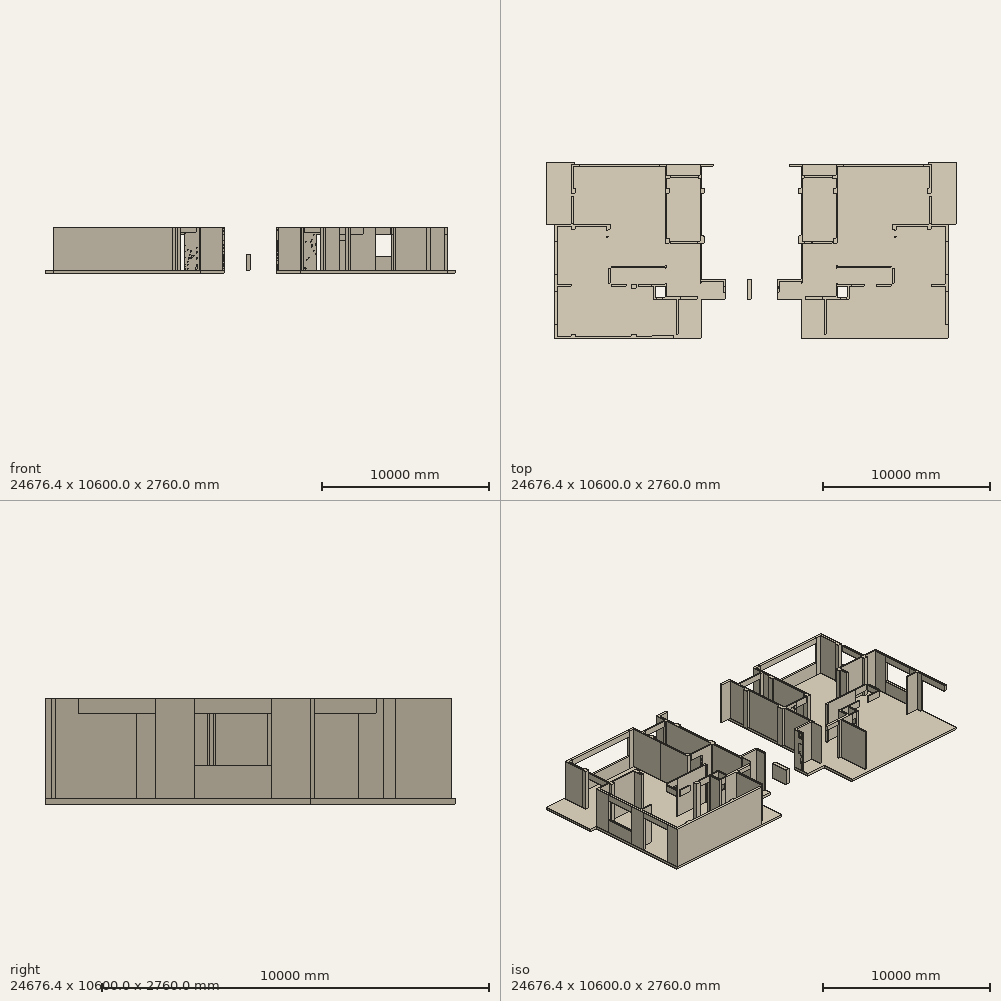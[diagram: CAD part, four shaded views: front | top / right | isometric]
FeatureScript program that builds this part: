
annotation { "Feature Type Name" : "Feature", "Feature Type Description" : "" }
export const myFeature = defineFeature(function(context is Context, id is Id, definition is map)
    precondition{}
    {
        {
            var Q0;
            Q0=qCreatedBy(makeId("Top.planeOp"),FACE);
            var sketch = newSketch(context, id + "F0", { "sketchPlane" : qUnion([Q0])});
            skLineSegment(sketch, "E0", {"start": v(-129.87, 2534.85) * mm, "end": v(8420.13, 2534.85) * mm});
            skLineSegment(sketch, "E1", {"start": v(-1879.16, 934.85) * mm, "end": v(11256.98, 934.85) * mm, "construction": true});
            skLineSegment(sketch, "E2", {"start": v(0, 1773.33) * mm, "end": v(0, -9278.74) * mm, "construction": true});
            skLineSegment(sketch, "E3", {"start": v(5650, -9203.63) * mm, "end": v(5650, -7807.62) * mm, "construction": true});
            skLineSegment(sketch, "E4.bottom", {"start": v(-125, 1084.85) * mm, "end": v(125, 1084.85) * mm});
            skLineSegment(sketch, "E4.top", {"start": v(-125, 784.85) * mm, "end": v(125, 784.85) * mm});
            skLineSegment(sketch, "E4.left", {"start": v(-125, 1084.85) * mm, "end": v(-125, 784.85) * mm});
            skLineSegment(sketch, "E4.right", {"start": v(125, 1084.85) * mm, "end": v(125, 784.85) * mm});
            skLineSegment(sketch, "E5.bottom", {"start": v(-125, 784.85) * mm, "end": v(-25, 784.85) * mm});
            skLineSegment(sketch, "E5.top", {"start": v(-125, 584.85) * mm, "end": v(-25, 584.85) * mm});
            skLineSegment(sketch, "E5.left", {"start": v(-125, 784.85) * mm, "end": v(-125, 584.85) * mm});
            skLineSegment(sketch, "E5.right", {"start": v(-25, 784.85) * mm, "end": v(-25, 584.85) * mm});
            skLineSegment(sketch, "E6.left", {"start": v(-125, 1084.85) * mm, "end": v(-129.87, 2534.85) * mm});
            skLineSegment(sketch, "E7.bottom", {"start": v(-129.87, 2534.85) * mm, "end": v(5170.13, 2534.85) * mm});
            skLineSegment(sketch, "E7.top", {"start": v(25, 2384.85) * mm, "end": v(5170.13, 2384.85) * mm});
            skLineSegment(sketch, "E7.right", {"start": v(5170.13, 2534.85) * mm, "end": v(5170.13, 2384.85) * mm});
            skLineSegment(sketch, "E8", {"start": v(370.13, 2534.85) * mm, "end": v(370.13, 2384.85) * mm});
            skLineSegment(sketch, "E9", {"start": v(5520.13, 2384.85) * mm, "end": v(5520.13, 126.86) * mm});
            skLineSegment(sketch, "E10", {"start": v(5520.13, 2534.85) * mm, "end": v(5620.13, 2534.85) * mm});
            skLineSegment(sketch, "E11", {"start": v(5620.13, 2534.85) * mm, "end": v(5620.13, 1834.85) * mm});
            skLineSegment(sketch, "E12", {"start": v(5620.13, 1834.85) * mm, "end": v(7620.13, 1834.85) * mm});
            skLineSegment(sketch, "E13", {"start": v(5620.13, 1684.85) * mm, "end": v(7725, 1684.85) * mm});
            skLineSegment(sketch, "E14", {"start": v(5620.13, 1684.85) * mm, "end": v(5620.13, 1084.85) * mm});
            skLineSegment(sketch, "E15.bottom", {"start": v(5520.13, 1084.85) * mm, "end": v(5859.5, 1084.85) * mm});
            skLineSegment(sketch, "E16", {"start": v(5170.13, 2384.85) * mm, "end": v(5520.13, 2384.85) * mm});
            skLineSegment(sketch, "E17.bottom", {"start": v(5520.13, 1084.85) * mm, "end": v(5770.13, 1084.85) * mm});
            skLineSegment(sketch, "E18", {"start": v(7620.13, 1834.85) * mm, "end": v(7620.13, 2534.85) * mm});
            skLineSegment(sketch, "E19", {"start": v(5820.13, 1684.85) * mm, "end": v(5820.13, 1834.85) * mm});
            skLineSegment(sketch, "E20", {"start": v(6720.13, 1684.85) * mm, "end": v(6720.13, 1834.85) * mm});
            skLineSegment(sketch, "E21", {"start": v(7520.13, 1834.85) * mm, "end": v(7520.13, 1684.85) * mm});
            skLineSegment(sketch, "E22", {"start": v(7720.13, 2384.85) * mm, "end": v(7720.13, 1084.85) * mm});
            skLineSegment(sketch, "E23", {"start": v(7720.13, 2384.85) * mm, "end": v(8420.13, 2384.85) * mm});
            skLineSegment(sketch, "E24", {"start": v(8420.13, 2534.85) * mm, "end": v(8420.13, 2384.85) * mm});
            skLineSegment(sketch, "E25", {"start": v(5520.13, 784.85) * mm, "end": v(5650, 784.85) * mm});
            skLineSegment(sketch, "E26", {"start": v(5650, 784.85) * mm, "end": v(5859.5, 784.85) * mm});
            skLineSegment(sketch, "E27.bottom", {"start": v(7725, 1084.85) * mm, "end": v(7875, 1084.85) * mm});
            skLineSegment(sketch, "E27.top", {"start": v(7725, 784.85) * mm, "end": v(7875, 784.85) * mm});
            skLineSegment(sketch, "E28", {"start": v(5620.13, 784.85) * mm, "end": v(5620.13, -143.22) * mm});
            skLineSegment(sketch, "E29", {"start": v(0, -1115.15) * mm, "end": v(2222.83, -1115.15) * mm});
            skLineSegment(sketch, "E30.top", {"start": v(-125, -1115.15) * mm, "end": v(-25, -1115.15) * mm});
            skLineSegment(sketch, "E30.left", {"start": v(-125, 584.85) * mm, "end": v(-125, -1115.15) * mm});
            skLineSegment(sketch, "E30.right", {"start": v(-25, 584.85) * mm, "end": v(-25, -1115.15) * mm});
            skLineSegment(sketch, "E31.top", {"start": v(-125, -1015.15) * mm, "end": v(-25, -1015.15) * mm});
            skLineSegment(sketch, "E31.left", {"start": v(-125, -1115.15) * mm, "end": v(-125, -1015.15) * mm});
            skLineSegment(sketch, "E31.right", {"start": v(-25, -1115.15) * mm, "end": v(-25, -1015.15) * mm});
            skLineSegment(sketch, "E32", {"start": v(-125, -115.15) * mm, "end": v(-25, -115.15) * mm});
            skLineSegment(sketch, "E33", {"start": v(-125, -1115.15) * mm, "end": v(-1125, -1115.15) * mm});
            skLineSegment(sketch, "E34", {"start": v(-1125, -1115.15) * mm, "end": v(-1125, -2115.15) * mm});
            skLineSegment(sketch, "E35", {"start": v(-975, -1215.15) * mm, "end": v(1972.83, -1215.15) * mm});
            skLineSegment(sketch, "E36.bottom", {"start": v(-125, -1115.15) * mm, "end": v(125, -1115.15) * mm});
            skLineSegment(sketch, "E36.top", {"start": v(-125, -1415.15) * mm, "end": v(125, -1415.15) * mm});
            skLineSegment(sketch, "E36.left", {"start": v(-125, -1115.15) * mm, "end": v(-125, -1415.15) * mm});
            skLineSegment(sketch, "E36.right", {"start": v(125, -1115.15) * mm, "end": v(125, -1415.15) * mm});
            skLineSegment(sketch, "E37", {"start": v(2222.83, -3615.15) * mm, "end": v(2222.83, -1115.15) * mm});
            skLineSegment(sketch, "E38", {"start": v(2122.83, -1415.15) * mm, "end": v(2122.83, -4715.15) * mm});
            skLineSegment(sketch, "E39.bottom", {"start": v(2222.83, -1115.15) * mm, "end": v(1972.83, -1115.15) * mm});
            skLineSegment(sketch, "E39.top", {"start": v(2222.83, -1415.15) * mm, "end": v(1972.83, -1415.15) * mm});
            skLineSegment(sketch, "E39.left", {"start": v(2222.83, -1115.15) * mm, "end": v(2222.83, -1415.15) * mm});
            skLineSegment(sketch, "E39.right", {"start": v(1972.83, -1115.15) * mm, "end": v(1972.83, -1415.15) * mm});
            skLineSegment(sketch, "E40", {"start": v(-129.87, 2534.85) * mm, "end": v(138.86, 2534.85) * mm});
            skLineSegment(sketch, "E41", {"start": v(25, 2634.85) * mm, "end": v(-1629.87, 2634.85) * mm});
            skLineSegment(sketch, "E42", {"start": v(25, 2534.85) * mm, "end": v(25, 2634.85) * mm});
            skLineSegment(sketch, "E43", {"start": v(-1125, -1115.15) * mm, "end": v(-1629.87, -1115.15) * mm});
            skLineSegment(sketch, "E44", {"start": v(-1629.87, -1115.15) * mm, "end": v(-1629.87, 2634.85) * mm});
            skLineSegment(sketch, "E45", {"start": v(-979.87, -4715.15) * mm, "end": v(2122.83, -4715.15) * mm});
            skLineSegment(sketch, "E46.bottom", {"start": v(-1125, -2115.15) * mm, "end": v(-979.87, -2115.15) * mm});
            skLineSegment(sketch, "E46.top", {"start": v(-1125, -4115.15) * mm, "end": v(-979.87, -4115.15) * mm});
            skLineSegment(sketch, "E46.left", {"start": v(-1125, -2115.15) * mm, "end": v(-1125, -4115.15) * mm});
            skLineSegment(sketch, "E46.right", {"start": v(-979.87, -2115.15) * mm, "end": v(-979.87, -4115.15) * mm});
            skLineSegment(sketch, "E47", {"start": v(-975, -1215.15) * mm, "end": v(-979.87, -2115.15) * mm});
            skLineSegment(sketch, "E48.top", {"start": v(-1125, -5115.15) * mm, "end": v(-979.87, -5115.15) * mm});
            skLineSegment(sketch, "E48.left", {"start": v(-1125, -4115.15) * mm, "end": v(-1125, -5115.15) * mm});
            skLineSegment(sketch, "E48.right", {"start": v(-979.87, -4115.15) * mm, "end": v(-979.87, -5115.15) * mm});
            skLineSegment(sketch, "E49.bottom", {"start": v(-979.87, -5115.15) * mm, "end": v(-1125, -5115.15) * mm});
            skLineSegment(sketch, "E49.top", {"start": v(-979.87, -7115.15) * mm, "end": v(-1125, -7115.15) * mm});
            skLineSegment(sketch, "E49.left", {"start": v(-979.87, -5115.15) * mm, "end": v(-979.87, -7115.15) * mm});
            skLineSegment(sketch, "E49.right", {"start": v(-1125, -5115.15) * mm, "end": v(-1125, -7115.15) * mm});
            skLineSegment(sketch, "E50.bottom", {"start": v(-1125, -7115.15) * mm, "end": v(-975, -7115.15) * mm});
            skLineSegment(sketch, "E50.left", {"start": v(-1125, -7115.15) * mm, "end": v(-1125, -7965.15) * mm});
            skLineSegment(sketch, "E50.right", {"start": v(-975, -7115.15) * mm, "end": v(-975, -7815.15) * mm});
            skLineSegment(sketch, "E51", {"start": v(-979.87, -4815.15) * mm, "end": v(-150, -4815.15) * mm});
            skLineSegment(sketch, "E52", {"start": v(2222.83, -3715.15) * mm, "end": v(2222.83, -4715.15) * mm});
            skLineSegment(sketch, "E53.bottom", {"start": v(-150, -4715.15) * mm, "end": v(150, -4715.15) * mm});
            skLineSegment(sketch, "E53.top", {"start": v(-150, -4965.15) * mm, "end": v(150, -4965.15) * mm});
            skLineSegment(sketch, "E53.left", {"start": v(-150, -4715.15) * mm, "end": v(-150, -4965.15) * mm});
            skLineSegment(sketch, "E53.right", {"start": v(150, -4715.15) * mm, "end": v(150, -4965.15) * mm});
            skLineSegment(sketch, "E54.bottom", {"start": v(-150, -7965.15) * mm, "end": v(150, -7965.15) * mm});
            skLineSegment(sketch, "E54.top", {"start": v(-150, -7715.15) * mm, "end": v(150, -7715.15) * mm});
            skLineSegment(sketch, "E54.left", {"start": v(-150, -7965.15) * mm, "end": v(-150, -7715.15) * mm});
            skLineSegment(sketch, "E54.right", {"start": v(150, -7965.15) * mm, "end": v(150, -7715.15) * mm});
            skLineSegment(sketch, "E55.trimOffspring", {"start": v(-150, -7815.15) * mm, "end": v(-975, -7815.15) * mm});
            skPoint(sketch, "E56.startSnap0", {"position": v(2222.83, -4215.15) * mm});
            skLineSegment(sketch, "E57", {"start": v(3220.13, -4815.15) * mm, "end": v(3220.13, -7815.15) * mm});
            skLineSegment(sketch, "E58", {"start": v(150, -4815.15) * mm, "end": v(3520.13, -4815.15) * mm});
            skLineSegment(sketch, "E59", {"start": v(2222.83, -4715.15) * mm, "end": v(5520.13, -4715.15) * mm});
            skLineSegment(sketch, "E60.trimOffspring", {"start": v(3820.13, -4815.15) * mm, "end": v(4820.13, -4815.15) * mm});
            skLineSegment(sketch, "E61", {"start": v(150, -7815.15) * mm, "end": v(3520.13, -7815.15) * mm});
            skLineSegment(sketch, "E62", {"start": v(3820.13, -4815.15) * mm, "end": v(3820.13, -7814.9) * mm});
            skLineSegment(sketch, "E63", {"start": v(3720.13, -4965.15) * mm, "end": v(3720.13, -7715.15) * mm});
            skLineSegment(sketch, "E64", {"start": v(-1125, -7965.15) * mm, "end": v(6320.13, -7965.15) * mm});
            skLineSegment(sketch, "E65", {"start": v(6320.13, -5615.15) * mm, "end": v(6320.13, -7804.95) * mm});
            skLineSegment(sketch, "E66", {"start": v(3820.13, -7814.9) * mm, "end": v(6020.13, -7806.15) * mm});
            skLineSegment(sketch, "E67", {"start": v(6220.13, -7715.15) * mm, "end": v(6220.13, -5615.15) * mm});
            skLineSegment(sketch, "E68", {"start": v(7725, 1684.85) * mm, "end": v(7725, 1084.85) * mm});
            skLineSegment(sketch, "E69.left", {"start": v(7725, 1084.85) * mm, "end": v(7725, 784.85) * mm});
            skLineSegment(sketch, "E70", {"start": v(2222.83, -3615.15) * mm, "end": v(5522.83, -3615.15) * mm});
            skLineSegment(sketch, "E71", {"start": v(2222.83, -3715.15) * mm, "end": v(5520.13, -3715.15) * mm});
            skLineSegment(sketch, "E72", {"start": v(5522.83, -3040.95) * mm, "end": v(5522.83, -3615.15) * mm});
            skLineSegment(sketch, "E73", {"start": v(5620.13, -4815.15) * mm, "end": v(5620.13, -2614.3) * mm});
            skPoint(sketch, "E74.trimOffspring.end.orphan", {"position": v(5520.13, -5415.07) * mm});
            skLineSegment(sketch, "E75", {"start": v(5520.13, -4715.15) * mm, "end": v(5520.13, -3715.15) * mm});
            skLineSegment(sketch, "E76", {"start": v(25, 2384.85) * mm, "end": v(25, 1084.85) * mm});
            skLineSegment(sketch, "E77", {"start": v(5520.13, 126.86) * mm, "end": v(5522.83, -3040.95) * mm});
            skLineSegment(sketch, "E78", {"start": v(5620.13, -143.22) * mm, "end": v(5620.13, -1915.15) * mm});
            skLineSegment(sketch, "E79.right", {"start": v(9025, -4814.81) * mm, "end": v(9025, -4539.81) * mm});
            skLineSegment(sketch, "E80", {"start": v(7948.57, -4539.81) * mm, "end": v(9025, -4539.81) * mm});
            skLineSegment(sketch, "E81.bottom", {"start": v(7625, 1084.85) * mm, "end": v(7875, 1084.85) * mm});
            skLineSegment(sketch, "E81.top", {"start": v(7625, 784.85) * mm, "end": v(7875, 784.85) * mm});
            skLineSegment(sketch, "E81.left", {"start": v(7625, 1084.85) * mm, "end": v(7625, 784.85) * mm});
            skLineSegment(sketch, "E81.right", {"start": v(7875, 1084.85) * mm, "end": v(7875, 784.85) * mm});
            skLineSegment(sketch, "E82.right", {"start": v(9025, -4739.81) * mm, "end": v(9025, -4539.81) * mm});
            skLineSegment(sketch, "E83", {"start": v(9125, -4539.81) * mm, "end": v(9125, -4439.81) * mm});
            skLineSegment(sketch, "E84", {"start": v(3920.13, -4715.15) * mm, "end": v(3920.13, -4815.15) * mm});
            skLineSegment(sketch, "E85.bottom", {"start": v(3920.13, -4715.15) * mm, "end": v(4720.13, -4715.15) * mm});
            skLineSegment(sketch, "E85.top", {"start": v(3920.13, -4815.15) * mm, "end": v(4720.13, -4815.15) * mm});
            skLineSegment(sketch, "E85.right", {"start": v(4720.13, -4715.15) * mm, "end": v(4720.13, -4815.15) * mm});
            skLineSegment(sketch, "E86.bottom", {"start": v(4920.13, -4815.15) * mm, "end": v(5520.13, -4815.15) * mm});
            skLineSegment(sketch, "E86.top", {"start": v(4820.13, -5615.15) * mm, "end": v(5520.13, -5615.15) * mm});
            skLineSegment(sketch, "E86.left", {"start": v(4820.13, -4815.15) * mm, "end": v(4820.13, -5615.15) * mm});
            skLineSegment(sketch, "E86.right", {"start": v(5520.13, -4815.15) * mm, "end": v(5520.13, -5515.15) * mm});
            skLineSegment(sketch, "E87.top", {"start": v(4920.13, -5515.15) * mm, "end": v(5520.13, -5515.15) * mm});
            skLineSegment(sketch, "E87.left", {"start": v(4920.13, -4815.15) * mm, "end": v(4920.13, -5515.15) * mm});
            skLineSegment(sketch, "E88.bottom", {"start": v(5520.13, -4815.15) * mm, "end": v(4920.13, -4815.15) * mm});
            skLineSegment(sketch, "E88.top", {"start": v(5620.13, -5615.15) * mm, "end": v(4820.13, -5615.15) * mm});
            skLineSegment(sketch, "E88.left", {"start": v(5620.13, -4815.15) * mm, "end": v(5620.13, -5439.81) * mm});
            skLineSegment(sketch, "E89", {"start": v(5620.13, -5615.15) * mm, "end": v(6220.13, -5615.15) * mm});
            skLineSegment(sketch, "E90.bottom", {"start": v(6320.13, -5615.15) * mm, "end": v(9125, -5615.15) * mm});
            skLineSegment(sketch, "E90.top", {"start": v(6220.13, -5439.81) * mm, "end": v(7620.13, -5439.81) * mm});
            skLineSegment(sketch, "E91.trimOffspring", {"start": v(6320.13, -5615.15) * mm, "end": v(6320.13, -7965.15) * mm});
            skLineSegment(sketch, "E92", {"start": v(7620.13, 1684.85) * mm, "end": v(7620.13, -5439.81) * mm});
            skLineSegment(sketch, "E93", {"start": v(7720.94, -5615.15) * mm, "end": v(7725, 784.85) * mm});
            skLineSegment(sketch, "E94", {"start": v(5770.13, 1084.85) * mm, "end": v(5770.13, 784.85) * mm});
            skLineSegment(sketch, "E95.bottom", {"start": v(5520.13, -5615.15) * mm, "end": v(5820.13, -5615.15) * mm});
            skLineSegment(sketch, "E95.left", {"start": v(5520.13, -5615.15) * mm, "end": v(5520.13, -5365.15) * mm});
            skLineSegment(sketch, "E96.trimOffspring", {"start": v(5620.13, -5439.81) * mm, "end": v(6320.13, -5439.81) * mm});
            skLineSegment(sketch, "E97.bottom", {"start": v(6320.13, -7965.15) * mm, "end": v(6020.13, -7965.15) * mm});
            skLineSegment(sketch, "E97.top", {"start": v(6320.13, -7715.15) * mm, "end": v(6020.13, -7715.15) * mm});
            skLineSegment(sketch, "E97.left", {"start": v(6320.13, -7965.15) * mm, "end": v(6320.13, -7715.15) * mm});
            skLineSegment(sketch, "E97.right", {"start": v(6020.13, -7965.15) * mm, "end": v(6020.13, -7715.15) * mm});
            skLineSegment(sketch, "E98", {"start": v(6320.13, -7965.15) * mm, "end": v(6770.13, -7965.15) * mm});
            skLineSegment(sketch, "E99", {"start": v(6770.13, -7965.15) * mm, "end": v(6770.13, -8264.5) * mm});
            skLineSegment(sketch, "E100", {"start": v(6320.13, -7815.15) * mm, "end": v(6920.13, -7815.15) * mm});
            skLineSegment(sketch, "E101", {"start": v(6920.13, -7815.15) * mm, "end": v(6920.13, -8027.96) * mm});
            skLineSegment(sketch, "E102", {"start": v(6470.13, -5439.81) * mm, "end": v(6470.13, -5615.15) * mm});
            skLineSegment(sketch, "E103.bottom", {"start": v(6470.13, -5439.81) * mm, "end": v(7470.13, -5439.81) * mm});
            skLineSegment(sketch, "E103.top", {"start": v(6470.13, -5615.15) * mm, "end": v(7470.13, -5615.15) * mm});
            skLineSegment(sketch, "E103.right", {"start": v(7470.13, -5439.81) * mm, "end": v(7470.13, -5615.15) * mm});
            skLineSegment(sketch, "E104", {"start": v(9125, -4539.81) * mm, "end": v(9125, -5615.15) * mm});
            skLineSegment(sketch, "E105", {"start": v(9025, -4814.81) * mm, "end": v(9025, -5439.81) * mm});
            skPoint(sketch, "E106.orphan", {"position": v(9125, -5439.81) * mm});
            skLineSegment(sketch, "E107", {"start": v(9125, -4439.81) * mm, "end": v(7721.68, -4439.81) * mm});
            skLineSegment(sketch, "E108", {"start": v(9025, -4539.81) * mm, "end": v(7721.62, -4539.81) * mm});
            skLineSegment(sketch, "E109.bottom", {"start": v(7620.13, -4639.81) * mm, "end": v(7721.11, -4639.81) * mm});
            skLineSegment(sketch, "E109.top", {"start": v(7620.13, -5339.81) * mm, "end": v(7721.11, -5339.81) * mm});
            skLineSegment(sketch, "E109.left", {"start": v(7620.13, -4639.81) * mm, "end": v(7620.13, -5339.81) * mm});
            skLineSegment(sketch, "E109.right", {"start": v(7721.11, -4639.81) * mm, "end": v(7721.11, -5339.81) * mm});
            skLineSegment(sketch, "E110.bottom", {"start": v(9025, -4814.81) * mm, "end": v(9125, -4814.81) * mm});
            skLineSegment(sketch, "E110.top", {"start": v(9025, -5164.81) * mm, "end": v(9125, -5164.81) * mm});
            skLineSegment(sketch, "E110.left", {"start": v(9025, -4814.81) * mm, "end": v(9025, -5164.81) * mm});
            skLineSegment(sketch, "E110.right", {"start": v(9125, -4814.81) * mm, "end": v(9125, -5164.81) * mm});
            skLineSegment(sketch, "E111", {"start": v(5772.12, -2115.15) * mm, "end": v(7620.13, -2115.15) * mm});
            skLineSegment(sketch, "E112", {"start": v(5620.13, -2215.15) * mm, "end": v(7620.13, -2215.15) * mm});
            skLineSegment(sketch, "E113.trimOffspring", {"start": v(7721.05, -5439.81) * mm, "end": v(9025, -5439.81) * mm});
            skLineSegment(sketch, "E114", {"start": v(5520.13, -4715.15) * mm, "end": v(5520.13, -4665.15) * mm});
            skLineSegment(sketch, "E115", {"start": v(5520.13, -4665.15) * mm, "end": v(5620.13, -4665.15) * mm});
            skLineSegment(sketch, "E116", {"start": v(5620.13, -4665.15) * mm, "end": v(5620.13, -3765.15) * mm});
            skLineSegment(sketch, "E117", {"start": v(5620.13, -3765.15) * mm, "end": v(5520.13, -3765.15) * mm});
            skLineSegment(sketch, "E118", {"start": v(5522.83, -3615.15) * mm, "end": v(5522.83, -3565.15) * mm});
            skLineSegment(sketch, "E119", {"start": v(5522.83, -3565.15) * mm, "end": v(5620.13, -3565.15) * mm});
            skLineSegment(sketch, "E120", {"start": v(5620.13, -3565.15) * mm, "end": v(5620.13, -2265.15) * mm});
            skLineSegment(sketch, "E121", {"start": v(5620.13, -2265.15) * mm, "end": v(5522.83, -2265.15) * mm});
            skLineSegment(sketch, "E122.bottom", {"start": v(5547.83, -3565.15) * mm, "end": v(5597.83, -3565.15) * mm});
            skLineSegment(sketch, "E122.top", {"start": v(5547.83, -2665.15) * mm, "end": v(5597.83, -2665.15) * mm});
            skLineSegment(sketch, "E122.left", {"start": v(5547.83, -3565.15) * mm, "end": v(5547.83, -2665.15) * mm});
            skLineSegment(sketch, "E122.right", {"start": v(5597.83, -3565.15) * mm, "end": v(5597.83, -2665.15) * mm});
            skLineSegment(sketch, "E123.top", {"start": v(5547.83, -2265.15) * mm, "end": v(5597.83, -2265.15) * mm});
            skLineSegment(sketch, "E123.left", {"start": v(5547.83, -2665.15) * mm, "end": v(5547.83, -2265.15) * mm});
            skLineSegment(sketch, "E123.right", {"start": v(5597.83, -2665.15) * mm, "end": v(5597.83, -2265.15) * mm});
            skLineSegment(sketch, "E124.bottom", {"start": v(5522.12, -2215.15) * mm, "end": v(5772.12, -2215.15) * mm});
            skLineSegment(sketch, "E124.top", {"start": v(5522.12, -1915.15) * mm, "end": v(5772.12, -1915.15) * mm});
            skLineSegment(sketch, "E124.left", {"start": v(5522.12, -2215.15) * mm, "end": v(5522.12, -1915.15) * mm});
            skLineSegment(sketch, "E124.right", {"start": v(5772.12, -2215.15) * mm, "end": v(5772.12, -1915.15) * mm});
            skLineSegment(sketch, "E125.trimOffspring", {"start": v(5620.13, -2215.15) * mm, "end": v(5620.13, -2614.3) * mm});
            skLineSegment(sketch, "E126", {"start": v(5822.12, -2215.15) * mm, "end": v(5822.12, -2115.15) * mm});
            skLineSegment(sketch, "E127.bottom", {"start": v(5822.12, -2115.15) * mm, "end": v(6722.12, -2115.15) * mm});
            skLineSegment(sketch, "E127.top", {"start": v(5822.12, -2215.15) * mm, "end": v(6722.12, -2215.15) * mm});
            skLineSegment(sketch, "E127.left", {"start": v(5822.12, -2115.15) * mm, "end": v(5822.12, -2215.15) * mm});
            skLineSegment(sketch, "E127.right", {"start": v(6722.12, -2115.15) * mm, "end": v(6722.12, -2215.15) * mm});
            skLineSegment(sketch, "E128.bottom", {"start": v(7500.13, -2115.15) * mm, "end": v(7620.13, -2115.15) * mm});
            skLineSegment(sketch, "E128.top", {"start": v(7500.13, -1665.15) * mm, "end": v(7620.13, -1665.15) * mm});
            skLineSegment(sketch, "E128.left", {"start": v(7500.13, -2115.15) * mm, "end": v(7500.13, -1665.15) * mm});
            skLineSegment(sketch, "E128.right", {"start": v(7620.13, -2115.15) * mm, "end": v(7620.13, -1665.15) * mm});
            skLineSegment(sketch, "E129", {"start": v(7560.13, -2179.43) * mm, "end": v(7560.13, -1551.21) * mm, "construction": true});
            skPoint(sketch, "E129.startSnap0", {"position": v(7560.13, -2115.15) * mm});
            skLineSegment(sketch, "E130", {"start": v(7560.13, -1551.21) * mm, "end": v(7560.13, -1665.15) * mm, "construction": true});
            skLineSegment(sketch, "E131", {"start": v(7560.13, -1665.15) * mm, "end": v(7560.13, -1725.15) * mm, "construction": true});
            skLineSegment(sketch, "E132", {"start": v(7560.13, -1725.15) * mm, "end": v(7786.33, -1725.15) * mm, "construction": true});
            skLineSegment(sketch, "E133", {"start": v(7786.33, -1835.15) * mm, "end": v(7399.39, -1835.15) * mm, "construction": true});
            skLineSegment(sketch, "E134", {"start": v(7399.39, -1945.15) * mm, "end": v(7797.2, -1945.15) * mm, "construction": true});
            skLineSegment(sketch, "E135", {"start": v(7797.2, -2055.15) * mm, "end": v(7386.08, -2055.15) * mm, "construction": true});
            skCircle(sketch, "E136", {"center": v(7560.13, -2055.15) * mm, "radius": 50 * mm});
            skCircle(sketch, "E137", {"center": v(7560.13, -1945.15) * mm, "radius": 50 * mm});
            skCircle(sketch, "E138", {"center": v(7560.13, -1835.15) * mm, "radius": 50 * mm});
            skCircle(sketch, "E139", {"center": v(7560.13, -1725.15) * mm, "radius": 50 * mm});
            skLineSegment(sketch, "E140.bottom", {"start": v(1972.83, -1415.15) * mm, "end": v(2122.83, -1415.15) * mm});
            skLineSegment(sketch, "E140.left", {"start": v(1972.83, -1415.15) * mm, "end": v(1972.83, -1535.15) * mm});
            skLineSegment(sketch, "E140.right", {"start": v(2122.83, -1415.15) * mm, "end": v(2122.83, -1535.15) * mm});
            skCircle(sketch, "E141", {"center": v(2047.7, -1475.15) * mm, "radius": 50 * mm});
            skLineSegment(sketch, "E142.bottom", {"start": v(7645.13, -5339.81) * mm, "end": v(7695.13, -5339.81) * mm});
            skLineSegment(sketch, "E142.top", {"start": v(7645.13, -4639.81) * mm, "end": v(7695.13, -4639.81) * mm});
            skLineSegment(sketch, "E142.left", {"start": v(7645.13, -5339.81) * mm, "end": v(7645.13, -4639.81) * mm});
            skLineSegment(sketch, "E142.right", {"start": v(7695.13, -5339.81) * mm, "end": v(7695.13, -4639.81) * mm});
            skLineSegment(sketch, "E143.bottom", {"start": v(6470.13, -5464.81) * mm, "end": v(7470.13, -5464.81) * mm});
            skLineSegment(sketch, "E143.top", {"start": v(6470.13, -5539.81) * mm, "end": v(7470.13, -5539.81) * mm});
            skLineSegment(sketch, "E143.left", {"start": v(6470.13, -5464.81) * mm, "end": v(6470.13, -5539.81) * mm});
            skLineSegment(sketch, "E143.right", {"start": v(7470.13, -5464.81) * mm, "end": v(7470.13, -5539.81) * mm});
            skLineSegment(sketch, "E144.bottom", {"start": v(4995.13, -5515.15) * mm, "end": v(5345.13, -5515.15) * mm});
            skLineSegment(sketch, "E144.top", {"start": v(4995.13, -5615.15) * mm, "end": v(5345.13, -5615.15) * mm});
            skLineSegment(sketch, "E144.left", {"start": v(4995.13, -5515.15) * mm, "end": v(4995.13, -5615.15) * mm});
            skLineSegment(sketch, "E144.right", {"start": v(5345.13, -5515.15) * mm, "end": v(5345.13, -5615.15) * mm});
            skLineSegment(sketch, "E145.bottom", {"start": v(3920.13, -4740.15) * mm, "end": v(4720.13, -4740.15) * mm});
            skLineSegment(sketch, "E145.top", {"start": v(3920.13, -4790.15) * mm, "end": v(4720.13, -4790.15) * mm});
            skLineSegment(sketch, "E145.left", {"start": v(3920.13, -4740.15) * mm, "end": v(3920.13, -4790.15) * mm});
            skLineSegment(sketch, "E145.right", {"start": v(4720.13, -4740.15) * mm, "end": v(4720.13, -4790.15) * mm});
            skLineSegment(sketch, "E146.bottom", {"start": v(2122.83, -3765.15) * mm, "end": v(2222.83, -3765.15) * mm});
            skLineSegment(sketch, "E146.top", {"start": v(2122.83, -4665.15) * mm, "end": v(2222.83, -4665.15) * mm});
            skLineSegment(sketch, "E146.left", {"start": v(2122.83, -3765.15) * mm, "end": v(2122.83, -4665.15) * mm});
            skLineSegment(sketch, "E146.right", {"start": v(2222.83, -3765.15) * mm, "end": v(2222.83, -4665.15) * mm});
            skLineSegment(sketch, "E147.bottom", {"start": v(2272.83, -3615.15) * mm, "end": v(3172.83, -3615.15) * mm});
            skLineSegment(sketch, "E147.top", {"start": v(2272.83, -3715.15) * mm, "end": v(3172.83, -3715.15) * mm});
            skLineSegment(sketch, "E147.left", {"start": v(2272.83, -3615.15) * mm, "end": v(2272.83, -3715.15) * mm});
            skLineSegment(sketch, "E147.right", {"start": v(3172.83, -3615.15) * mm, "end": v(3172.83, -3715.15) * mm});
            skLineSegment(sketch, "E148.bottom", {"start": v(2272.83, -4815.15) * mm, "end": v(3172.83, -4815.15) * mm});
            skLineSegment(sketch, "E148.top", {"start": v(2272.83, -4715.15) * mm, "end": v(3172.83, -4715.15) * mm});
            skLineSegment(sketch, "E148.left", {"start": v(2272.83, -4815.15) * mm, "end": v(2272.83, -4715.15) * mm});
            skLineSegment(sketch, "E148.right", {"start": v(3172.83, -4815.15) * mm, "end": v(3172.83, -4715.15) * mm});
            skLineSegment(sketch, "E149.bottom", {"start": v(2272.83, -4740.15) * mm, "end": v(3172.83, -4740.15) * mm});
            skLineSegment(sketch, "E149.top", {"start": v(2272.83, -4790.15) * mm, "end": v(3172.83, -4790.15) * mm});
            skLineSegment(sketch, "E149.left", {"start": v(2272.83, -4740.15) * mm, "end": v(2272.83, -4790.15) * mm});
            skLineSegment(sketch, "E149.right", {"start": v(3172.83, -4740.15) * mm, "end": v(3172.83, -4790.15) * mm});
            skLineSegment(sketch, "E150.bottom", {"start": v(2147.83, -3765.15) * mm, "end": v(2197.83, -3765.15) * mm});
            skLineSegment(sketch, "E150.top", {"start": v(2147.83, -4665.15) * mm, "end": v(2197.83, -4665.15) * mm});
            skLineSegment(sketch, "E150.left", {"start": v(2147.83, -3765.15) * mm, "end": v(2147.83, -4665.15) * mm});
            skLineSegment(sketch, "E150.right", {"start": v(2197.83, -3765.15) * mm, "end": v(2197.83, -4665.15) * mm});
            skLineSegment(sketch, "E151.bottom", {"start": v(6770.13, -8264.5) * mm, "end": v(6920.13, -8264.5) * mm});
            skLineSegment(sketch, "E151.top", {"start": v(6770.13, -7815.15) * mm, "end": v(6920.13, -7815.15) * mm});
            skLineSegment(sketch, "E151.left", {"start": v(6770.13, -8264.5) * mm, "end": v(6770.13, -7965.15) * mm});
            skLineSegment(sketch, "E151.right", {"start": v(6920.13, -8264.5) * mm, "end": v(6920.13, -7815.15) * mm});
            skLineSegment(sketch, "E152.bottom", {"start": v(3820.13, -4715.15) * mm, "end": v(3520.13, -4715.15) * mm});
            skLineSegment(sketch, "E152.top", {"start": v(3820.13, -4965.15) * mm, "end": v(3520.13, -4965.15) * mm});
            skLineSegment(sketch, "E152.left", {"start": v(3820.13, -4715.15) * mm, "end": v(3820.13, -4965.15) * mm});
            skLineSegment(sketch, "E152.right", {"start": v(3520.13, -4715.15) * mm, "end": v(3520.13, -4965.15) * mm});
            skLineSegment(sketch, "E153.bottom", {"start": v(3820.13, -7965.15) * mm, "end": v(3520.13, -7965.15) * mm});
            skLineSegment(sketch, "E153.top", {"start": v(3820.13, -7715.15) * mm, "end": v(3520.13, -7715.15) * mm});
            skLineSegment(sketch, "E153.left", {"start": v(3820.13, -7965.15) * mm, "end": v(3820.13, -7715.15) * mm});
            skLineSegment(sketch, "E153.right", {"start": v(3520.13, -7965.15) * mm, "end": v(3520.13, -7715.15) * mm});
            skLineSegment(sketch, "E154.bottom", {"start": v(3600.34, -5415.37) * mm, "end": v(3720.34, -5415.37) * mm});
            skLineSegment(sketch, "E154.top", {"start": v(3600.34, -4965.37) * mm, "end": v(3720.34, -4965.37) * mm});
            skLineSegment(sketch, "E154.left", {"start": v(3600.34, -5415.37) * mm, "end": v(3600.34, -4965.37) * mm});
            skLineSegment(sketch, "E154.right", {"start": v(3720.34, -5415.37) * mm, "end": v(3720.34, -4965.37) * mm});
            skPoint(sketch, "E155.startSnap0", {"position": v(3660.34, -5415.37) * mm});
            skLineSegment(sketch, "E156", {"start": v(3660.34, -5025.37) * mm, "end": v(3660.34, -6093.24) * mm, "construction": true});
            skCircle(sketch, "E157", {"center": v(3660.34, -5355.37) * mm, "radius": 50 * mm});
            skCircle(sketch, "E158", {"center": v(3660.34, -5245.37) * mm, "radius": 50 * mm});
            skCircle(sketch, "E159", {"center": v(3660.34, -5135.37) * mm, "radius": 50 * mm});
            skCircle(sketch, "E160", {"center": v(3660.34, -5025.37) * mm, "radius": 50 * mm});
            skLineSegment(sketch, "E161.bottom", {"start": v(1988.55, -1864.75) * mm, "end": v(2111.78, -1864.75) * mm});
            skLineSegment(sketch, "E161.top", {"start": v(1988.55, -1414.75) * mm, "end": v(2111.78, -1414.75) * mm});
            skLineSegment(sketch, "E161.right", {"start": v(2111.78, -1415.15) * mm, "end": v(2111.78, -1414.75) * mm});
            skPoint(sketch, "E162.startSnap0", {"position": v(2050.16, -1864.75) * mm});
            skCircle(sketch, "E163", {"center": v(2048.55, -1804.75) * mm, "radius": 50 * mm});
            skCircle(sketch, "E164", {"center": v(2048.55, -1694.75) * mm, "radius": 50 * mm});
            skCircle(sketch, "E165", {"center": v(2048.55, -1584.75) * mm, "radius": 50 * mm});
            skCircle(sketch, "E166", {"center": v(2048.55, -1474.75) * mm, "radius": 50 * mm});
            skLineSegment(sketch, "E167.top", {"start": v(1972.83, -1864.75) * mm, "end": v(2122.83, -1864.75) * mm});
            skLineSegment(sketch, "E167.left", {"start": v(1972.83, -1415.15) * mm, "end": v(1972.83, -1864.75) * mm});
            skLineSegment(sketch, "E167.right", {"start": v(2122.83, -1415.15) * mm, "end": v(2122.83, -1864.75) * mm});
            skLineSegment(sketch, "E168.bottom", {"start": v(7620.13, -2215.15) * mm, "end": v(7870.13, -2215.15) * mm});
            skLineSegment(sketch, "E168.left", {"start": v(7620.13, -2215.15) * mm, "end": v(7620.13, -1665.15) * mm});
            skLineSegment(sketch, "E168.right", {"start": v(7870.13, -2215.15) * mm, "end": v(7870.13, -1793.35) * mm});
            skLineSegment(sketch, "E169", {"start": v(7620.13, -1786.8) * mm, "end": v(7870.13, -1793.35) * mm});
            skLineSegment(sketch, "E170.bottom", {"start": v(5522.12, -2215.15) * mm, "end": v(5620.13, -2215.15) * mm});
            skLineSegment(sketch, "E170.top", {"start": v(5522.12, -2265.15) * mm, "end": v(5620.13, -2265.15) * mm});
            skLineSegment(sketch, "E170.left", {"start": v(5522.12, -2215.15) * mm, "end": v(5522.12, -2265.15) * mm});
            skLineSegment(sketch, "E170.right", {"start": v(5620.13, -2215.15) * mm, "end": v(5620.13, -2265.15) * mm});
            skSolve(sketch);
        }
        {
            var Q0;
            {var subQ1=sQuery(id+"F0.wireOp",EDGE,"E39.bottom");Q0=makeQuery(id+"F0.imprint","IMPRINT",FACE,{"disambiguationData":[TD([[makeQuery(id+"F0.imprint","IMPRINT",EDGE,{"derivedFrom":subQ1}),1.0]])]});}
            var Q1;
            {var subQ5=sQuery(id+"F0.wireOp",EDGE,"E36.top");Q1=makeQuery(id+"F0.imprint","IMPRINT",FACE,{"disambiguationData":[TD([[makeQuery(id+"F0.imprint","IMPRINT",EDGE,{"derivedFrom":subQ5}),1.0]])]});}
            var Q2;
            {var subQ1=sQuery(id+"F0.wireOp",EDGE,"E36.bottom");var subQ3=makeQuery(id+"F0.imprint","IMPRINT",VERTEX,{"derivedFrom":subQ1});Q2=makeQuery(id+"F0.imprint","IMPRINT",FACE,{"disambiguationData":[TD([[makeQuery(id+"F0.imprint","IMPRINT",EDGE,{"disambiguationData":[TD([[subQ3,1.0]])],"derivedFrom":subQ1}),-1.0]])]});}
            var Q3;
            {var subQ3=sQuery(id+"F0.wireOp",EDGE,"E53.bottom");Q3=makeQuery(id+"F0.imprint","IMPRINT",FACE,{"disambiguationData":[TD([[makeQuery(id+"F0.imprint","IMPRINT",EDGE,{"derivedFrom":subQ3}),-1.0]])]});}
            var Q4;
            {var subQ5=sQuery(id+"F0.wireOp",EDGE,"E54.top");Q4=makeQuery(id+"F0.imprint","IMPRINT",FACE,{"disambiguationData":[TD([[makeQuery(id+"F0.imprint","IMPRINT",EDGE,{"derivedFrom":subQ5}),-1.0]])]});}
            var Q5;
            Q5=makeQuery(id+"F0.imprint","IMPRINT",FACE,{"disambiguationData":[TD([[makeQuery(id+"F0.imprint","IMPRINT",EDGE,{"derivedFrom":sQuery(id+"F0.wireOp",EDGE,"E4.top")}),1.0]])]});
            var Q6;
            {var subQ7=sQuery(id+"F0.wireOp",EDGE,"E94");Q6=makeQuery(id+"F0.imprint","IMPRINT",FACE,{"disambiguationData":[TD([[makeQuery(id+"F0.imprint","IMPRINT",EDGE,{"derivedFrom":subQ7}),-1.0]])]});}
            var Q7;
            {var subQ4=sQuery(id+"F0.wireOp",EDGE,"E124.left");Q7=makeQuery(id+"F0.imprint","IMPRINT",FACE,{"disambiguationData":[TD([[makeQuery(id+"F0.imprint","IMPRINT",EDGE,{"derivedFrom":subQ4}),-1.0]])]});}
            var Q8;
            {var subQ0=sQuery(id+"F0.wireOp",EDGE,"E69.left");Q8=makeQuery(id+"F0.imprint","IMPRINT",FACE,{"disambiguationData":[TD([[makeQuery(id+"F0.imprint","IMPRINT",EDGE,{"derivedFrom":subQ0}),1.0]])]});}
            var Q9;
            {var subQ1=sQuery(id+"F0.wireOp",EDGE,"E69.left");Q9=makeQuery(id+"F0.imprint","IMPRINT",FACE,{"disambiguationData":[TD([[makeQuery(id+"F0.imprint","IMPRINT",EDGE,{"derivedFrom":subQ1}),-1.0]])]});}
            var Q10;
            {var subQ1=sQuery(id+"F0.wireOp",EDGE,"E97.bottom");Q10=makeQuery(id+"F0.imprint","IMPRINT",FACE,{"disambiguationData":[TD([[makeQuery(id+"F0.imprint","IMPRINT",EDGE,{"derivedFrom":subQ1}),-1.0]])]});}
            var Q11;
            {var subQ2=sQuery(id+"F0.wireOp",EDGE,"E153.bottom");Q11=makeQuery(id+"F0.imprint","IMPRINT",FACE,{"disambiguationData":[TD([[makeQuery(id+"F0.imprint","IMPRINT",EDGE,{"derivedFrom":subQ2}),-1.0]])]});}
            var Q12;
            {var subQ2=sQuery(id+"F0.wireOp",EDGE,"E152.bottom");Q12=makeQuery(id+"F0.imprint","IMPRINT",FACE,{"disambiguationData":[TD([[makeQuery(id+"F0.imprint","IMPRINT",EDGE,{"derivedFrom":subQ2}),1.0]])]});}
            var Q13;
            {var subQ1=sQuery(id+"F0.wireOp",EDGE,"E128.bottom");Q13=makeQuery(id+"F0.imprint","IMPRINT",FACE,{"disambiguationData":[TD([[makeQuery(id+"F0.imprint","IMPRINT",EDGE,{"derivedFrom":subQ1}),1.0]])]});}
            var Q14;
            {var subQ4=sQuery(id+"F0.wireOp",EDGE,"E168.bottom");var subQ6=sQuery(id+"F0.wireOp",EDGE,"E93");var subQ7=makeQuery(id+"F0.imprint","INTERSECT",VERTEX,{"derivedFrom":[subQ6,subQ4]});Q14=makeQuery(id+"F0.imprint","IMPRINT",FACE,{"disambiguationData":[TD([[makeQuery(id+"F0.imprint","IMPRINT",EDGE,{"disambiguationData":[TD([[subQ7,-1.0]])],"derivedFrom":subQ6}),1.0]])]});}
            var Q15;
            {var subQ5=sQuery(id+"F0.wireOp",EDGE,"E168.right");Q15=makeQuery(id+"F0.imprint","IMPRINT",FACE,{"disambiguationData":[TD([[makeQuery(id+"F0.imprint","IMPRINT",EDGE,{"derivedFrom":subQ5}),1.0]])]});}
            var Q16;
            Q16=makeQuery(id+"F0.imprint","IMPRINT",FACE,{"disambiguationData":[TD([[makeQuery(id+"F0.imprint","IMPRINT",EDGE,{"derivedFrom":sQuery(id+"F0.wireOp",EDGE,"E163")}),-1.0]])]});
            var Q17;
            {var subQ5=sQuery(id+"F0.wireOp",EDGE,"E50.left");Q17=makeQuery(id+"F0.imprint","IMPRINT",FACE,{"disambiguationData":[TD([[makeQuery(id+"F0.imprint","IMPRINT",EDGE,{"derivedFrom":subQ5}),1.0]])]});}
            var Q18;
            {var subQ3=sQuery(id+"F0.wireOp",EDGE,"E46.top");Q18=makeQuery(id+"F0.imprint","IMPRINT",FACE,{"disambiguationData":[TD([[makeQuery(id+"F0.imprint","IMPRINT",EDGE,{"derivedFrom":subQ3}),-1.0]])]});}
            var Q19;
            {var subQ5=sQuery(id+"F0.wireOp",EDGE,"E51");Q19=makeQuery(id+"F0.imprint","IMPRINT",FACE,{"disambiguationData":[TD([[makeQuery(id+"F0.imprint","IMPRINT",EDGE,{"derivedFrom":subQ5}),1.0]])]});}
            var Q20;
            {var subQ0=sQuery(id+"F0.wireOp",EDGE,"E64");var subQ1=sQuery(id+"F0.wireOp",EDGE,"E54.right");var subQ2=makeQuery(id+"F0.imprint","INTERSECT",VERTEX,{"derivedFrom":[subQ1,subQ0]});Q20=makeQuery(id+"F0.imprint","IMPRINT",FACE,{"disambiguationData":[TD([[makeQuery(id+"F0.imprint","IMPRINT",EDGE,{"disambiguationData":[TD([[subQ2,-1.0]])],"derivedFrom":subQ1}),-1.0]])]});}
            var Q21;
            {var subQ1=sQuery(id+"F0.wireOp",EDGE,"E62");Q21=makeQuery(id+"F0.imprint","IMPRINT",FACE,{"disambiguationData":[TD([[makeQuery(id+"F0.imprint","IMPRINT",EDGE,{"derivedFrom":subQ1}),-1.0]])]});}
            var Q22;
            {var subQ3=sQuery(id+"F0.wireOp",EDGE,"E145.left");Q22=makeQuery(id+"F0.imprint","IMPRINT",FACE,{"disambiguationData":[TD([[makeQuery(id+"F0.imprint","IMPRINT",EDGE,{"derivedFrom":subQ3}),-1.0]])]});}
            var Q23;
            {var subQ8=sQuery(id+"F0.wireOp",EDGE,"E67");Q23=makeQuery(id+"F0.imprint","IMPRINT",FACE,{"disambiguationData":[TD([[makeQuery(id+"F0.imprint","IMPRINT",EDGE,{"derivedFrom":subQ8}),-1.0]])]});}
            var Q24;
            {var subQ3=sQuery(id+"F0.wireOp",EDGE,"E144.right");Q24=makeQuery(id+"F0.imprint","IMPRINT",FACE,{"disambiguationData":[TD([[makeQuery(id+"F0.imprint","IMPRINT",EDGE,{"derivedFrom":subQ3}),1.0]])]});}
            var Q25;
            {var subQ5=sQuery(id+"F0.wireOp",EDGE,"E66");Q25=makeQuery(id+"F0.imprint","IMPRINT",FACE,{"disambiguationData":[TD([[makeQuery(id+"F0.imprint","IMPRINT",EDGE,{"derivedFrom":subQ5}),-1.0]])]});}
            var Q26;
            {var subQ0=sQuery(id+"F0.wireOp",EDGE,"E142.bottom");Q26=makeQuery(id+"F0.imprint","IMPRINT",FACE,{"disambiguationData":[TD([[makeQuery(id+"F0.imprint","IMPRINT",EDGE,{"derivedFrom":subQ0}),-1.0]])]});}
            var Q27;
            Q27=makeQuery(id+"F0.imprint","IMPRINT",FACE,{"disambiguationData":[TD([[makeQuery(id+"F0.imprint","IMPRINT",EDGE,{"derivedFrom":sQuery(id+"F0.wireOp",EDGE,"E105")}),1.0]])]});
            var Q28;
            Q28=makeQuery(id+"F0.imprint","IMPRINT",FACE,{"disambiguationData":[TD([[makeQuery(id+"F0.imprint","IMPRINT",EDGE,{"derivedFrom":sQuery(id+"F0.wireOp",EDGE,"E79.right")}),-1.0]])]});
            var Q29;
            {var subQ9=sQuery(id+"F0.wireOp",EDGE,"E109.right");Q29=makeQuery(id+"F0.imprint","IMPRINT",FACE,{"disambiguationData":[TD([[makeQuery(id+"F0.imprint","IMPRINT",EDGE,{"derivedFrom":subQ9}),1.0]])]});}
            var Q30;
            {var subQ3=sQuery(id+"F0.wireOp",EDGE,"E81.left");Q30=makeQuery(id+"F0.imprint","IMPRINT",FACE,{"disambiguationData":[TD([[makeQuery(id+"F0.imprint","IMPRINT",EDGE,{"derivedFrom":subQ3}),-1.0]])]});}
            var Q31;
            {var subQ3=sQuery(id+"F0.wireOp",EDGE,"E149.right");Q31=makeQuery(id+"F0.imprint","IMPRINT",FACE,{"disambiguationData":[TD([[makeQuery(id+"F0.imprint","IMPRINT",EDGE,{"derivedFrom":subQ3}),1.0]])]});}
            var Q32;
            {var subQ3=sQuery(id+"F0.wireOp",EDGE,"E149.left");Q32=makeQuery(id+"F0.imprint","IMPRINT",FACE,{"disambiguationData":[TD([[makeQuery(id+"F0.imprint","IMPRINT",EDGE,{"derivedFrom":subQ3}),-1.0]])]});}
            var Q33;
            {var subQ7=sQuery(id+"F0.wireOp",EDGE,"E37");Q33=makeQuery(id+"F0.imprint","IMPRINT",FACE,{"disambiguationData":[TD([[makeQuery(id+"F0.imprint","IMPRINT",EDGE,{"derivedFrom":subQ7}),1.0]])]});}
            var Q34;
            {var subQ3=sQuery(id+"F0.wireOp",EDGE,"E117");Q34=makeQuery(id+"F0.imprint","IMPRINT",FACE,{"disambiguationData":[TD([[makeQuery(id+"F0.imprint","IMPRINT",EDGE,{"derivedFrom":subQ3}),-1.0]])]});}
            var Q35;
            {var subQ8=sQuery(id+"F0.wireOp",EDGE,"E7.right");Q35=makeQuery(id+"F0.imprint","IMPRINT",FACE,{"disambiguationData":[TD([[makeQuery(id+"F0.imprint","IMPRINT",EDGE,{"derivedFrom":subQ8}),1.0]])]});}
            var Q36;
            {var subQ8=sQuery(id+"F0.wireOp",EDGE,"E18");Q36=makeQuery(id+"F0.imprint","IMPRINT",FACE,{"disambiguationData":[TD([[makeQuery(id+"F0.imprint","IMPRINT",EDGE,{"derivedFrom":subQ8}),-1.0]])]});}
            var Q37;
            {var subQ6=sQuery(id+"F0.wireOp",EDGE,"E6.left");Q37=makeQuery(id+"F0.imprint","IMPRINT",FACE,{"disambiguationData":[TD([[makeQuery(id+"F0.imprint","IMPRINT",EDGE,{"derivedFrom":subQ6}),-1.0]])]});}
            var Q38;
            Q38=makeQuery(id+"F0.imprint","IMPRINT",FACE,{"disambiguationData":[TD([[makeQuery(id+"F0.imprint","IMPRINT",EDGE,{"derivedFrom":sQuery(id+"F0.wireOp",EDGE,"E31.top")}),-1.0]])]});
            var Q39;
            Q39=makeQuery(id+"F0.imprint","IMPRINT",FACE,{"disambiguationData":[TD([[makeQuery(id+"F0.imprint","IMPRINT",EDGE,{"derivedFrom":sQuery(id+"F0.wireOp",EDGE,"E5.bottom")}),-1.0]])]});
            var Q40;
            {var subQ4=sQuery(id+"F0.wireOp",EDGE,"E28");Q40=makeQuery(id+"F0.imprint","IMPRINT",FACE,{"disambiguationData":[TD([[makeQuery(id+"F0.imprint","IMPRINT",EDGE,{"derivedFrom":subQ4}),-1.0]])]});}
            var Q41;
            {var subQ0=sQuery(id+"F0.wireOp",EDGE,"E29");Q41=makeQuery(id+"F0.imprint","IMPRINT",FACE,{"disambiguationData":[TD([[makeQuery(id+"F0.imprint","IMPRINT",EDGE,{"derivedFrom":subQ0}),-1.0]])]});}
            var Q42;
            {var subQ1=sQuery(id+"F0.wireOp",EDGE,"E33");Q42=makeQuery(id+"F0.imprint","IMPRINT",FACE,{"disambiguationData":[TD([[makeQuery(id+"F0.imprint","IMPRINT",EDGE,{"derivedFrom":subQ1}),1.0]])]});}
            var Q43;
            {var subQ3=sQuery(id+"F0.wireOp",EDGE,"E127.left");Q43=makeQuery(id+"F0.imprint","IMPRINT",FACE,{"disambiguationData":[TD([[makeQuery(id+"F0.imprint","IMPRINT",EDGE,{"derivedFrom":subQ3}),-1.0]])]});}
            var Q44;
            {var subQ4=sQuery(id+"F0.wireOp",EDGE,"E127.right");Q44=makeQuery(id+"F0.imprint","IMPRINT",FACE,{"disambiguationData":[TD([[makeQuery(id+"F0.imprint","IMPRINT",EDGE,{"derivedFrom":subQ4}),1.0]])]});}
            var Q45;
            {var subQ5=sQuery(id+"F0.wireOp",EDGE,"E170.bottom");Q45=makeQuery(id+"F0.imprint","IMPRINT",FACE,{"disambiguationData":[TD([[makeQuery(id+"F0.imprint","IMPRINT",EDGE,{"derivedFrom":subQ5}),-1.0]])]});}
            extrude(context, id + "F1", {"entities" : qUnion([Q0, Q1, Q2, Q3, Q4, Q5, Q6, Q7, Q8, Q9, Q10, Q11, Q12, Q13, Q14, Q15, Q16, Q17, Q18, Q19, Q20, Q21, Q22, Q23, Q24, Q25, Q26, Q27, Q28, Q29, Q30, Q31, Q32, Q33, Q34, Q35, Q36, Q37, Q38, Q39, Q40, Q41, Q42, Q43, Q44, Q45]), "depth" : 2600 * mm});
        }
        {
            var Q0;
            {var subQ0=sQuery(id+"F0.wireOp",EDGE,"E7.right");Q0=makeQuery(id+"F0.imprint","IMPRINT",FACE,{"disambiguationData":[TD([[makeQuery(id+"F0.imprint","IMPRINT",EDGE,{"derivedFrom":subQ0}),-1.0]])]});}
            var Q1;
            Q1=makeQuery(id+"F0.imprint","IMPRINT",FACE,{"disambiguationData":[TD([[makeQuery(id+"F0.imprint","IMPRINT",EDGE,{"derivedFrom":sQuery(id+"F0.wireOp",EDGE,"E46.bottom")}),-1.0]])]});
            var Q2;
            Q2=makeQuery(id+"F0.imprint","IMPRINT",FACE,{"disambiguationData":[TD([[makeQuery(id+"F0.imprint","IMPRINT",EDGE,{"derivedFrom":sQuery(id+"F0.wireOp",EDGE,"E49.bottom")}),1.0]])]});
            extrude(context, id + "F2", {"entities" : qUnion([Q0, Q1, Q2]), "depth" : 850 * mm});
        }
        {
            var Q0;
            Q0=makeQuery(id+"F1.opExtrude","CAP_FACE",FACE,{"disambiguationData":[OSD([sQuery(id+"F0.wireOp",EDGE,"E50.bottom"),sQuery(id+"F0.wireOp",EDGE,"E50.left"),sQuery(id+"F0.wireOp",EDGE,"E50.right"),sQuery(id+"F0.wireOp",EDGE,"E54.top"),sQuery(id+"F0.wireOp",EDGE,"E54.left"),sQuery(id+"F0.wireOp",EDGE,"E54.right"),sQuery(id+"F0.wireOp",EDGE,"E55.trimOffspring"),sQuery(id+"F0.wireOp",EDGE,"E58"),sQuery(id+"F0.wireOp",EDGE,"E59"),sQuery(id+"F0.wireOp",EDGE,"E60.trimOffspring"),sQuery(id+"F0.wireOp",EDGE,"E61"),sQuery(id+"F0.wireOp",EDGE,"E62"),sQuery(id+"F0.wireOp",EDGE,"E63"),sQuery(id+"F0.wireOp",EDGE,"E64"),sQuery(id+"F0.wireOp",EDGE,"E66"),sQuery(id+"F0.wireOp",EDGE,"E67"),sQuery(id+"F0.wireOp",EDGE,"E73"),sQuery(id+"F0.wireOp",EDGE,"E84"),sQuery(id+"F0.wireOp",EDGE,"E85.right"),sQuery(id+"F0.wireOp",EDGE,"E87.top"),sQuery(id+"F0.wireOp",EDGE,"E87.left"),sQuery(id+"F0.wireOp",EDGE,"E86.right"),sQuery(id+"F0.wireOp",EDGE,"E88.top"),sQuery(id+"F0.wireOp",EDGE,"E88.left"),sQuery(id+"F0.wireOp",EDGE,"E86.left"),sQuery(id+"F0.wireOp",EDGE,"E86.bottom"),sQuery(id+"F0.wireOp",EDGE,"E89"),sQuery(id+"F0.wireOp",EDGE,"E90.bottom"),sQuery(id+"F0.wireOp",EDGE,"E90.top"),sQuery(id+"F0.wireOp",EDGE,"E91.trimOffspring"),sQuery(id+"F0.wireOp",EDGE,"E95.bottom"),sQuery(id+"F0.wireOp",EDGE,"E95.left"),sQuery(id+"F0.wireOp",EDGE,"E96.trimOffspring"),sQuery(id+"F0.wireOp",EDGE,"E97.bottom"),sQuery(id+"F0.wireOp",EDGE,"E97.top"),sQuery(id+"F0.wireOp",EDGE,"E97.left"),sQuery(id+"F0.wireOp",EDGE,"E97.right"),sQuery(id+"F0.wireOp",EDGE,"E102"),sQuery(id+"F0.wireOp",EDGE,"E114"),sQuery(id+"F0.wireOp",EDGE,"E115"),sQuery(id+"F0.wireOp",EDGE,"E143.left"),sQuery(id+"F0.wireOp",EDGE,"E144.left"),sQuery(id+"F0.wireOp",EDGE,"E144.right"),sQuery(id+"F0.wireOp",EDGE,"E145.left"),sQuery(id+"F0.wireOp",EDGE,"E145.right"),sQuery(id+"F0.wireOp",EDGE,"E148.right"),sQuery(id+"F0.wireOp",EDGE,"E149.right"),sQuery(id+"F0.wireOp",EDGE,"E152.bottom"),sQuery(id+"F0.wireOp",EDGE,"E152.top"),sQuery(id+"F0.wireOp",EDGE,"E152.left"),sQuery(id+"F0.wireOp",EDGE,"E152.right"),sQuery(id+"F0.wireOp",EDGE,"E153.bottom"),sQuery(id+"F0.wireOp",EDGE,"E153.top"),sQuery(id+"F0.wireOp",EDGE,"E153.left"),sQuery(id+"F0.wireOp",EDGE,"E153.right"),sQuery(id+"F0.wireOp",EDGE,"E154.bottom"),sQuery(id+"F0.wireOp",EDGE,"E154.top"),sQuery(id+"F0.wireOp",EDGE,"E154.right")])],"isStart":true});
            var sketch = newSketch(context, id + "F3", { "sketchPlane" : qUnion([Q0])});
            skLineSegment(sketch, "E171.0", {"start": v(-1125, 7965.15) * mm, "end": v(6320.13, 7965.15) * mm});
            skLineSegment(sketch, "E172.0", {"start": v(7470.13, 5615.15) * mm, "end": v(9125, 5615.15) * mm});
            skLineSegment(sketch, "E173.0", {"start": v(9125, 4439.81) * mm, "end": v(7721.68, 4439.81) * mm});
            skLineSegment(sketch, "E174.0", {"start": v(9125, 5164.81) * mm, "end": v(9125, 5615.15) * mm});
            skLineSegment(sketch, "E175.0", {"start": v(9125, 4439.81) * mm, "end": v(9125, 4814.81) * mm});
            skLineSegment(sketch, "E176.bottom", {"start": v(7721.68, 4439.81) * mm, "end": v(9125, 4439.81) * mm});
            skLineSegment(sketch, "E176.top", {"start": v(7721.68, 5615.15) * mm, "end": v(9125, 5615.15) * mm});
            skLineSegment(sketch, "E176.right", {"start": v(9125, 4439.81) * mm, "end": v(9125, 5615.15) * mm});
            skLineSegment(sketch, "E177.0", {"start": v(7720.13, -2384.85) * mm, "end": v(7720.13, -1084.85) * mm});
            skLineSegment(sketch, "E178.0", {"start": v(7620.13, -2534.85) * mm, "end": v(8420.13, -2534.85) * mm});
            skLineSegment(sketch, "E179.bottom", {"start": v(-1125, 7965.15) * mm, "end": v(7720.13, 7965.15) * mm});
            skLineSegment(sketch, "E179.top", {"start": v(-1125, -2534.85) * mm, "end": v(7720.13, -2534.85) * mm});
            skLineSegment(sketch, "E179.left", {"start": v(-1125, 7965.15) * mm, "end": v(-1125, -2534.85) * mm});
            skLineSegment(sketch, "E179.right", {"start": v(7720.13, 7965.15) * mm, "end": v(7720.13, 5615.15) * mm});
            skLineSegment(sketch, "E180.right", {"start": v(9125, 5615.15) * mm, "end": v(9125, 4439.81) * mm});
            skLineSegment(sketch, "E181.trimOffspring", {"start": v(7720.13, -1084.85) * mm, "end": v(7720.13, -2534.85) * mm});
            skLineSegment(sketch, "E182", {"start": v(7721.68, 4439.81) * mm, "end": v(7720.13, -2534.85) * mm});
            skLineSegment(sketch, "E183.0", {"start": v(-125, 1115.15) * mm, "end": v(-1125, 1115.15) * mm});
            skLineSegment(sketch, "E184", {"start": v(-1125, 1115.15) * mm, "end": v(-1625, 1115.15) * mm});
            skLineSegment(sketch, "E185", {"start": v(-1625, 1115.15) * mm, "end": v(-1625, -2534.85) * mm});
            skLineSegment(sketch, "E186", {"start": v(-1625, -2534.85) * mm, "end": v(-1625, -2634.85) * mm});
            skLineSegment(sketch, "E187", {"start": v(-1625, -2634.85) * mm, "end": v(-125, -2634.85) * mm});
            skLineSegment(sketch, "E188", {"start": v(-125, -2634.85) * mm, "end": v(75, -2634.85) * mm});
            skLineSegment(sketch, "E189", {"start": v(75, -2634.85) * mm, "end": v(75, -2534.85) * mm});
            skSolve(sketch);
        }
        {
            var Q0;
            Q0 = qSketchRegion(id + "F3", true);
            extrude(context, id + "F4", {"entities" : qUnion([Q0]), "depth" : 160 * mm});
        }
        {
            var Q0;
            Q0=makeQuery(id+"F1.opExtrude","SWEPT_FACE",FACE,{"disambiguationData":[OSD([sQuery(id+"F0.wireOp",EDGE,"E104")])]});
            var sketch = newSketch(context, id + "F5", { "sketchPlane" : qUnion([Q0])});
            skLineSegment(sketch, "E190.0", {"start": v(-4814.81, 2600) * mm, "end": v(-4814.81, 0) * mm});
            skLineSegment(sketch, "E191.bottom", {"start": v(-5164.81, 2600) * mm, "end": v(-4814.81, 2600) * mm});
            skLineSegment(sketch, "E191.top", {"start": v(-5164.81, 2200) * mm, "end": v(-4814.81, 2200) * mm});
            skLineSegment(sketch, "E191.left", {"start": v(-5164.81, 2600) * mm, "end": v(-5164.81, 2200) * mm});
            skLineSegment(sketch, "E191.right", {"start": v(-4814.81, 2600) * mm, "end": v(-4814.81, 2200) * mm});
            skLineSegment(sketch, "E192.bottom", {"start": v(-5164.81, 0) * mm, "end": v(-4814.81, 0) * mm});
            skLineSegment(sketch, "E192.top", {"start": v(-5164.81, 1800) * mm, "end": v(-4814.81, 1800) * mm});
            skLineSegment(sketch, "E192.left", {"start": v(-5164.81, 0) * mm, "end": v(-5164.81, 1800) * mm});
            skLineSegment(sketch, "E192.right", {"start": v(-4814.81, 0) * mm, "end": v(-4814.81, 1800) * mm});
            skSolve(sketch);
        }
        {
            var Q0;
            Q0 = qSketchRegion(id + "F5", true);
            extrude(context, id + "F6", {"entities" : qUnion([Q0]), "oppositeDirection" : true, "depth" : 100 * mm});
        }
        {
            var Q0;
            Q0=makeQuery(id+"F1.opExtrude","SWEPT_FACE",FACE,{"disambiguationData":[OSD([sQuery(id+"F0.wireOp",EDGE,"E88.top"),sQuery(id+"F0.wireOp",EDGE,"E89"),sQuery(id+"F0.wireOp",EDGE,"E95.bottom")])]});
            var sketch = newSketch(context, id + "F7", { "sketchPlane" : qUnion([Q0])});
            skLineSegment(sketch, "E193.bottom", {"start": v(4998.47, 0) * mm, "end": v(5345.13, 0) * mm});
            skLineSegment(sketch, "E193.top", {"start": v(4998.47, 1800) * mm, "end": v(5345.13, 1800) * mm});
            skLineSegment(sketch, "E193.left", {"start": v(4998.47, 0) * mm, "end": v(4998.47, 1800) * mm});
            skLineSegment(sketch, "E193.right", {"start": v(5345.13, 0) * mm, "end": v(5345.13, 1800) * mm});
            skLineSegment(sketch, "E194.bottom", {"start": v(5345.13, 2600) * mm, "end": v(4998.47, 2600) * mm});
            skLineSegment(sketch, "E194.top", {"start": v(5345.13, 2200) * mm, "end": v(4998.47, 2200) * mm});
            skLineSegment(sketch, "E194.left", {"start": v(5345.13, 2600) * mm, "end": v(5345.13, 2200) * mm});
            skLineSegment(sketch, "E194.right", {"start": v(4998.47, 2600) * mm, "end": v(4998.47, 2200) * mm});
            skSolve(sketch);
        }
        {
            var Q0;
            Q0 = qSketchRegion(id + "F7", true);
            extrude(context, id + "F8", {"entities" : qUnion([Q0]), "oppositeDirection" : true, "depth" : 100 * mm});
        }
        {
            var Q0;
            Q0=makeQuery(id+"F4.opExtrude","CAP_FACE",FACE,{"disambiguationData":[OSD([sQuery(id+"F3.wireOp",EDGE,"E172.0"),sQuery(id+"F3.wireOp",EDGE,"E179.bottom"),sQuery(id+"F3.wireOp",EDGE,"E179.top"),sQuery(id+"F3.wireOp",EDGE,"E179.left"),sQuery(id+"F3.wireOp",EDGE,"E179.right"),sQuery(id+"F3.wireOp",EDGE,"E176.top"),sQuery(id+"F3.wireOp",EDGE,"E176.bottom"),sQuery(id+"F3.wireOp",EDGE,"E180.right"),sQuery(id+"F3.wireOp",EDGE,"E182")])],"isStart":true});
            var sketch = newSketch(context, id + "F9", { "sketchPlane" : qUnion([Q0])});
            skLineSegment(sketch, "E195.0", {"start": v(4920.13, -4815.15) * mm, "end": v(5520.13, -4815.15) * mm});
            skLineSegment(sketch, "E196.0", {"start": v(4920.13, -4815.15) * mm, "end": v(4920.13, -5515.15) * mm});
            skLineSegment(sketch, "E197.0", {"start": v(5520.13, -4815.15) * mm, "end": v(5520.13, -5515.15) * mm});
            skLineSegment(sketch, "E198.bottom", {"start": v(5520.13, -5515.15) * mm, "end": v(4920.13, -5515.15) * mm});
            skLineSegment(sketch, "E198.top", {"start": v(5520.13, -4815.15) * mm, "end": v(4920.13, -4815.15) * mm});
            skLineSegment(sketch, "E198.left", {"start": v(5520.13, -5515.15) * mm, "end": v(5520.13, -4815.15) * mm});
            skLineSegment(sketch, "E198.right", {"start": v(4920.13, -5515.15) * mm, "end": v(4920.13, -4815.15) * mm});
            skSolve(sketch);
        }
        {
            var Q0;
            Q0 = qSketchRegion(id + "F9", true);
            extrude(context, id + "F10", {"entities" : qUnion([Q0]), "operationType" : NewBodyOperationType.REMOVE, "oppositeDirection" : true, "depth" : 160 * mm});
        }
        {
            var Q0;
            Q0=makeQuery(id+"F1.opExtrude","SWEPT_FACE",FACE,{"disambiguationData":[OSD([sQuery(id+"F0.wireOp",EDGE,"E34")])]});
            var sketch = newSketch(context, id + "F11", { "sketchPlane" : qUnion([Q0])});
            skLineSegment(sketch, "E199.0", {"start": v(2115.15, 2600) * mm, "end": v(2115.15, 0) * mm});
            skLineSegment(sketch, "E200.0", {"start": v(3765.15, 2200) * mm, "end": v(3765.15, 2190.3) * mm});
            skLineSegment(sketch, "E201.0", {"start": v(1864.75, 2600) * mm, "end": v(3765.15, 2600) * mm});
            skLineSegment(sketch, "E202.0", {"start": v(5415.37, 2600) * mm, "end": v(7715.15, 2600) * mm});
            skLineSegment(sketch, "E203.0", {"start": v(5115.15, 2600) * mm, "end": v(5115.15, 0) * mm});
            skLineSegment(sketch, "E204.0", {"start": v(7115.15, 2600) * mm, "end": v(7115.15, 0) * mm});
            skLineSegment(sketch, "E205.bottom", {"start": v(2115.15, 2600) * mm, "end": v(3765.15, 2600) * mm});
            skLineSegment(sketch, "E205.top", {"start": v(2115.15, 2200) * mm, "end": v(3765.15, 2200) * mm});
            skLineSegment(sketch, "E205.left", {"start": v(2115.15, 2600) * mm, "end": v(2115.15, 2200) * mm});
            skLineSegment(sketch, "E206.bottom", {"start": v(5115.15, 2600) * mm, "end": v(7115.15, 2600) * mm});
            skLineSegment(sketch, "E206.top", {"start": v(5115.15, 2200) * mm, "end": v(7115.15, 2200) * mm});
            skLineSegment(sketch, "E206.left", {"start": v(5115.15, 2600) * mm, "end": v(5115.15, 2200) * mm});
            skLineSegment(sketch, "E206.right", {"start": v(7115.15, 2600) * mm, "end": v(7115.15, 2200) * mm});
            skLineSegment(sketch, "E207.bottom", {"start": v(2115.15, 2600) * mm, "end": v(4115.15, 2600) * mm});
            skLineSegment(sketch, "E207.top", {"start": v(2115.15, 2190.3) * mm, "end": v(4115.15, 2190.3) * mm});
            skLineSegment(sketch, "E207.left", {"start": v(2115.15, 2600) * mm, "end": v(2115.15, 2190.3) * mm});
            skLineSegment(sketch, "E207.right", {"start": v(4115.15, 2600) * mm, "end": v(4115.15, 2190.3) * mm});
            skPoint(sketch, "E208.orphan", {"position": v(3765.15, 0) * mm});
            skSolve(sketch);
        }
        {
            var Q0;
            Q0 = qSketchRegion(id + "F11", true);
            extrude(context, id + "F12", {"entities" : qUnion([Q0]), "oppositeDirection" : true, "depth" : 150 * mm});
        }
        {
            var Q0;
            Q0=makeQuery(id+"F1.opExtrude","SWEPT_FACE",FACE,{"disambiguationData":[OSD([sQuery(id+"F0.wireOp",EDGE,"E4.left"),sQuery(id+"F0.wireOp",EDGE,"E5.left")])]});
            var sketch = newSketch(context, id + "F13", { "sketchPlane" : qUnion([Q0])});
            skLineSegment(sketch, "E209.0", {"start": v(1015.15, 2600) * mm, "end": v(1015.15, 0) * mm});
            skLineSegment(sketch, "E210.bottom", {"start": v(-584.85, 2600) * mm, "end": v(1015.15, 2600) * mm});
            skLineSegment(sketch, "E210.top", {"start": v(-584.85, 2200) * mm, "end": v(1015.15, 2200) * mm});
            skLineSegment(sketch, "E210.left", {"start": v(-584.85, 2600) * mm, "end": v(-584.85, 2200) * mm});
            skLineSegment(sketch, "E210.right", {"start": v(1015.15, 2600) * mm, "end": v(1015.15, 2200) * mm});
            skSolve(sketch);
        }
        {
            var Q0;
            Q0 = qSketchRegion(id + "F13", true);
            extrude(context, id + "F14", {"entities" : qUnion([Q0]), "oppositeDirection" : true, "depth" : 100 * mm});
        }
        {
            var Q0;
            Q0=makeQuery(id+"F1.opExtrude","SWEPT_FACE",FACE,{"disambiguationData":[OSD([sQuery(id+"F0.wireOp",EDGE,"E0"),sQuery(id+"F0.wireOp",EDGE,"E10")])]});
            var sketch = newSketch(context, id + "F15", { "sketchPlane" : qUnion([Q0])});
            skLineSegment(sketch, "E211.0", {"start": v(-5170.13, 2600) * mm, "end": v(-5170.13, 0) * mm});
            skLineSegment(sketch, "E212.0", {"start": v(-370.13, 2600) * mm, "end": v(-370.13, 0) * mm});
            skLineSegment(sketch, "E213.bottom", {"start": v(-5170.13, 2200) * mm, "end": v(-370.13, 2200) * mm});
            skLineSegment(sketch, "E213.top", {"start": v(-5170.13, 2600) * mm, "end": v(-370.13, 2600) * mm});
            skLineSegment(sketch, "E213.left", {"start": v(-5170.13, 2200) * mm, "end": v(-5170.13, 2600) * mm});
            skLineSegment(sketch, "E213.right", {"start": v(-370.13, 2200) * mm, "end": v(-370.13, 2600) * mm});
            skSolve(sketch);
        }
        {
            var Q0;
            Q0 = qSketchRegion(id + "F15", true);
            extrude(context, id + "F16", {"entities" : qUnion([Q0]), "oppositeDirection" : true, "depth" : 150 * mm});
        }
        {
            var Q0;
            {var subQ0=sQuery(id+"F0.wireOp",EDGE,"E12");Q0=makeQuery(id+"F1.opExtrude","SWEPT_FACE",FACE,{"disambiguationData":[OSD([subQ0]),TDD([makeQuery(id+"F0.imprint","IMPRINT",EDGE,{"disambiguationData":[TD([[makeQuery(id+"F0.imprint","INTERSECT",VERTEX,{"derivedFrom":[sQuery(id+"F0.wireOp",EDGE,"E11"),subQ0]}),-1.0]])],"derivedFrom":subQ0})])]});}
            var sketch = newSketch(context, id + "F17", { "sketchPlane" : qUnion([Q0])});
            skLineSegment(sketch, "E214.0", {"start": v(-7520.13, 2600) * mm, "end": v(-7520.13, 0) * mm});
            skLineSegment(sketch, "E215.0", {"start": v(-5820.13, 2600) * mm, "end": v(-5820.13, 0) * mm});
            skLineSegment(sketch, "E216.bottom", {"start": v(-7520.13, 2600) * mm, "end": v(-5820.13, 2600) * mm});
            skLineSegment(sketch, "E216.top", {"start": v(-7520.13, 2200) * mm, "end": v(-5820.13, 2200) * mm});
            skLineSegment(sketch, "E216.left", {"start": v(-7520.13, 2600) * mm, "end": v(-7520.13, 2200) * mm});
            skLineSegment(sketch, "E216.right", {"start": v(-5820.13, 2600) * mm, "end": v(-5820.13, 2200) * mm});
            skSolve(sketch);
        }
        {
            var Q0;
            Q0 = qSketchRegion(id + "F17", true);
            extrude(context, id + "F18", {"entities" : qUnion([Q0]), "oppositeDirection" : true, "depth" : 100 * mm});
        }
        {
            var Q0;
            {var subQ0=sQuery(id+"F0.wireOp",EDGE,"E111");Q0=makeQuery(id+"F1.opExtrude","SWEPT_FACE",FACE,{"disambiguationData":[OSD([subQ0]),TDD([makeQuery(id+"F0.imprint","IMPRINT",EDGE,{"disambiguationData":[TD([[makeQuery(id+"F0.imprint","INTERSECT",VERTEX,{"derivedFrom":[subQ0,sQuery(id+"F0.wireOp",EDGE,"E128.bottom"),sQuery(id+"F0.wireOp",EDGE,"E128.left")]}),1.0]])],"derivedFrom":subQ0})])]});}
            var sketch = newSketch(context, id + "F19", { "sketchPlane" : qUnion([Q0])});
            skLineSegment(sketch, "E217.0.0", {"start": v(-7500.13, 0) * mm, "end": v(-6722.12, 0) * mm});
            skLineSegment(sketch, "E217.0.1", {"start": v(-6722.12, 0) * mm, "end": v(-6722.12, 2600) * mm});
            skLineSegment(sketch, "E217.0.2", {"start": v(-6722.12, 2600) * mm, "end": v(-7500.13, 2600) * mm});
            skLineSegment(sketch, "E217.0.3", {"start": v(-7500.13, 2600) * mm, "end": v(-7500.13, 0) * mm});
            skLineSegment(sketch, "E218.bottom", {"start": v(-6722.12, 2600) * mm, "end": v(-5822.12, 2600) * mm});
            skLineSegment(sketch, "E218.top", {"start": v(-6722.12, 2200) * mm, "end": v(-5822.12, 2200) * mm});
            skLineSegment(sketch, "E218.left", {"start": v(-6722.12, 2600) * mm, "end": v(-6722.12, 2200) * mm});
            skLineSegment(sketch, "E218.right", {"start": v(-5822.12, 2600) * mm, "end": v(-5822.12, 2200) * mm});
            skSolve(sketch);
        }
        {
            var Q0;
            Q0 = qSketchRegion(id + "F19", true);
            extrude(context, id + "F20", {"entities" : qUnion([Q0]), "oppositeDirection" : true, "depth" : 100 * mm});
        }
        {
            var Q0;
            {var subQ0=sQuery(id+"F0.wireOp",EDGE,"E70");Q0=makeQuery(id+"F1.opExtrude","SWEPT_FACE",FACE,{"disambiguationData":[OSD([subQ0]),TDD([makeQuery(id+"F0.imprint","IMPRINT",EDGE,{"disambiguationData":[TD([[makeQuery(id+"F0.imprint","INTERSECT",VERTEX,{"derivedFrom":[subQ0,sQuery(id+"F0.wireOp",EDGE,"E118")]}),1.0]])],"derivedFrom":subQ0})])]});}
            var sketch = newSketch(context, id + "F21", { "sketchPlane" : qUnion([Q0])});
            skLineSegment(sketch, "E219.0", {"start": v(-2272.83, 2600) * mm, "end": v(-2272.83, 0) * mm});
            skLineSegment(sketch, "E220.0", {"start": v(-3172.83, 2600) * mm, "end": v(-3172.83, 0) * mm});
            skLineSegment(sketch, "E221.bottom", {"start": v(-3172.83, 2600) * mm, "end": v(-2272.83, 2600) * mm});
            skLineSegment(sketch, "E221.top", {"start": v(-3172.83, 2200) * mm, "end": v(-2272.83, 2200) * mm});
            skLineSegment(sketch, "E221.left", {"start": v(-3172.83, 2600) * mm, "end": v(-3172.83, 2200) * mm});
            skLineSegment(sketch, "E221.right", {"start": v(-2272.83, 2600) * mm, "end": v(-2272.83, 2200) * mm});
            skSolve(sketch);
        }
        {
            var Q0;
            Q0 = qSketchRegion(id + "F21", true);
            extrude(context, id + "F22", {"entities" : qUnion([Q0]), "oppositeDirection" : true, "depth" : 100 * mm});
        }
        {
            var Q0;
            {var subQ0=sQuery(id+"F0.wireOp",EDGE,"E59");Q0=makeQuery(id+"F1.opExtrude","SWEPT_FACE",FACE,{"disambiguationData":[OSD([subQ0]),TDD([makeQuery(id+"F0.imprint","IMPRINT",EDGE,{"disambiguationData":[TD([[makeQuery(id+"F0.imprint","INTERSECT",VERTEX,{"derivedFrom":[subQ0,sQuery(id+"F0.wireOp",EDGE,"E114")]}),1.0]])],"derivedFrom":subQ0})])]});}
            var sketch = newSketch(context, id + "F23", { "sketchPlane" : qUnion([Q0])});
            skLineSegment(sketch, "E222.0", {"start": v(-4720.13, 2600) * mm, "end": v(-4720.13, 0) * mm});
            skLineSegment(sketch, "E223.0", {"start": v(-3920.13, 2600) * mm, "end": v(-3920.13, 0) * mm});
            skLineSegment(sketch, "E224.0", {"start": v(-3172.83, 2600) * mm, "end": v(-3172.83, 0) * mm});
            skLineSegment(sketch, "E225.0", {"start": v(-2272.83, 2600) * mm, "end": v(-2272.83, 0) * mm});
            skLineSegment(sketch, "E226.bottom", {"start": v(-4720.13, 2600) * mm, "end": v(-3920.13, 2600) * mm});
            skLineSegment(sketch, "E226.top", {"start": v(-4720.13, 2200) * mm, "end": v(-3920.13, 2200) * mm});
            skLineSegment(sketch, "E226.left", {"start": v(-4720.13, 2600) * mm, "end": v(-4720.13, 2200) * mm});
            skLineSegment(sketch, "E226.right", {"start": v(-3920.13, 2600) * mm, "end": v(-3920.13, 2200) * mm});
            skLineSegment(sketch, "E227.bottom", {"start": v(-3172.83, 2600) * mm, "end": v(-2272.83, 2600) * mm});
            skLineSegment(sketch, "E227.top", {"start": v(-3172.83, 2200) * mm, "end": v(-2272.83, 2200) * mm});
            skLineSegment(sketch, "E227.left", {"start": v(-3172.83, 2600) * mm, "end": v(-3172.83, 2200) * mm});
            skLineSegment(sketch, "E227.right", {"start": v(-2272.83, 2600) * mm, "end": v(-2272.83, 2200) * mm});
            skSolve(sketch);
        }
        {
            var Q0;
            Q0 = qSketchRegion(id + "F23", true);
            extrude(context, id + "F24", {"entities" : qUnion([Q0]), "oppositeDirection" : true, "depth" : 100 * mm});
        }
        {
            var Q0;
            Q0=makeQuery(id+"F1.opExtrude","SWEPT_FACE",FACE,{"disambiguationData":[OSD([sQuery(id+"F0.wireOp",EDGE,"E90.top"),sQuery(id+"F0.wireOp",EDGE,"E96.trimOffspring")])]});
            var sketch = newSketch(context, id + "F25", { "sketchPlane" : qUnion([Q0])});
            skLineSegment(sketch, "E228.0", {"start": v(-6470.13, 2600) * mm, "end": v(-6470.13, 0) * mm});
            skLineSegment(sketch, "E229.0", {"start": v(-7470.13, 2600) * mm, "end": v(-7470.13, 0) * mm});
            skLineSegment(sketch, "E230.bottom", {"start": v(-6470.13, 2600) * mm, "end": v(-7470.13, 2600) * mm});
            skLineSegment(sketch, "E230.top", {"start": v(-6470.13, 2300) * mm, "end": v(-7470.13, 2300) * mm});
            skLineSegment(sketch, "E230.left", {"start": v(-6470.13, 2600) * mm, "end": v(-6470.13, 2300) * mm});
            skLineSegment(sketch, "E230.right", {"start": v(-7470.13, 2600) * mm, "end": v(-7470.13, 2300) * mm});
            skSolve(sketch);
        }
        {
            var Q0;
            Q0 = qSketchRegion(id + "F25", true);
            extrude(context, id + "F26", {"entities" : qUnion([Q0]), "oppositeDirection" : true, "depth" : 150 * mm});
        }
        {
            var Q0;
            Q0=makeQuery(id+"F1.opExtrude","SWEPT_FACE",FACE,{"disambiguationData":[OSD([sQuery(id+"F0.wireOp",EDGE,"E37"),sQuery(id+"F0.wireOp",EDGE,"E39.left")])]});
            var sketch = newSketch(context, id + "F27", { "sketchPlane" : qUnion([Q0])});
            skLineSegment(sketch, "E231.0.0", {"start": v(-3615.15, 0) * mm, "end": v(-1115.15, 0) * mm});
            skLineSegment(sketch, "E231.0.1", {"start": v(-1115.15, 0) * mm, "end": v(-1115.15, 2600) * mm});
            skLineSegment(sketch, "E231.0.2", {"start": v(-1115.15, 2600) * mm, "end": v(-3615.15, 2600) * mm});
            skLineSegment(sketch, "E231.0.3", {"start": v(-3615.15, 2600) * mm, "end": v(-3615.15, 0) * mm});
            skLineSegment(sketch, "E232.0", {"start": v(-3765.15, 2600) * mm, "end": v(-3765.15, 0) * mm});
            skLineSegment(sketch, "E233.0", {"start": v(-4665.15, 2600) * mm, "end": v(-4665.15, 0) * mm});
            skLineSegment(sketch, "E234.bottom", {"start": v(-4665.15, 2600) * mm, "end": v(-3765.15, 2600) * mm});
            skLineSegment(sketch, "E234.top", {"start": v(-4665.15, 2200) * mm, "end": v(-3765.15, 2200) * mm});
            skLineSegment(sketch, "E234.left", {"start": v(-4665.15, 2600) * mm, "end": v(-4665.15, 2200) * mm});
            skLineSegment(sketch, "E234.right", {"start": v(-3765.15, 2600) * mm, "end": v(-3765.15, 2200) * mm});
            skSolve(sketch);
        }
        {
            var Q0;
            Q0=makeQuery(id+"F27.imprint","IMPRINT",FACE,{"disambiguationData":[TD([[makeQuery(id+"F27.imprint","IMPRINT",EDGE,{"derivedFrom":sQuery(id+"F27.wireOp",EDGE,"E234.bottom")}),-1.0]])]});
            extrude(context, id + "F28", {"entities" : qUnion([Q0]), "oppositeDirection" : true, "depth" : 100 * mm});
        }
        {
            var Q0;
            Q0=makeQuery(id+"F4.opExtrude","CAP_FACE",FACE,{"disambiguationData":[OSD([sQuery(id+"F3.wireOp",EDGE,"E172.0"),sQuery(id+"F3.wireOp",EDGE,"E179.bottom"),sQuery(id+"F3.wireOp",EDGE,"E179.top"),sQuery(id+"F3.wireOp",EDGE,"E179.left"),sQuery(id+"F3.wireOp",EDGE,"E179.right"),sQuery(id+"F3.wireOp",EDGE,"E176.top"),sQuery(id+"F3.wireOp",EDGE,"E176.bottom"),sQuery(id+"F3.wireOp",EDGE,"E180.right"),sQuery(id+"F3.wireOp",EDGE,"E182"),sQuery(id+"F3.wireOp",EDGE,"E184"),sQuery(id+"F3.wireOp",EDGE,"E185"),sQuery(id+"F3.wireOp",EDGE,"E186"),sQuery(id+"F3.wireOp",EDGE,"E187"),sQuery(id+"F3.wireOp",EDGE,"E188"),sQuery(id+"F3.wireOp",EDGE,"E189")])],"isStart":true});
            var sketch = newSketch(context, id + "F29", { "sketchPlane" : qUnion([Q0])});
            skLineSegment(sketch, "E235.bottom", {"start": v(10464.76, -5615.15) * mm, "end": v(10713.2, -5615.15) * mm});
            skLineSegment(sketch, "E235.top", {"start": v(10464.76, -4439.81) * mm, "end": v(10713.2, -4439.81) * mm});
            skLineSegment(sketch, "E235.left", {"start": v(10464.76, -5615.15) * mm, "end": v(10464.76, -4439.81) * mm});
            skLineSegment(sketch, "E235.right", {"start": v(10713.2, -5615.15) * mm, "end": v(10713.2, -4439.81) * mm});
            skSolve(sketch);
        }
        {
            var Q0;
            Q0 = qSketchRegion(id + "F29", true);
            extrude(context, id + "F30", {"entities" : qUnion([Q0]), "depth" : 1000 * mm});
        }
        {
            var Q0;
            Q0=makeQuery(id+"F1.opExtrude","SWEPT_BODY",BODY,{"disambiguationData":[OSD([sQuery(id+"F0.wireOp",EDGE,"E0"),sQuery(id+"F0.wireOp",EDGE,"E7.right"),sQuery(id+"F0.wireOp",EDGE,"E9"),sQuery(id+"F0.wireOp",EDGE,"E10"),sQuery(id+"F0.wireOp",EDGE,"E11"),sQuery(id+"F0.wireOp",EDGE,"E12"),sQuery(id+"F0.wireOp",EDGE,"E13"),sQuery(id+"F0.wireOp",EDGE,"E14"),sQuery(id+"F0.wireOp",EDGE,"E16"),sQuery(id+"F0.wireOp",EDGE,"E17.bottom"),sQuery(id+"F0.wireOp",EDGE,"E19"),sQuery(id+"F0.wireOp",EDGE,"E25"),sQuery(id+"F0.wireOp",EDGE,"E26"),sQuery(id+"F0.wireOp",EDGE,"E28"),sQuery(id+"F0.wireOp",EDGE,"E77"),sQuery(id+"F0.wireOp",EDGE,"E78"),sQuery(id+"F0.wireOp",EDGE,"E94"),sQuery(id+"F0.wireOp",EDGE,"E111"),sQuery(id+"F0.wireOp",EDGE,"E112"),sQuery(id+"F0.wireOp",EDGE,"E124.bottom"),sQuery(id+"F0.wireOp",EDGE,"E124.top"),sQuery(id+"F0.wireOp",EDGE,"E124.right"),sQuery(id+"F0.wireOp",EDGE,"E127.left"),sQuery(id+"F0.wireOp",EDGE,"E170.top"),sQuery(id+"F0.wireOp",EDGE,"E170.right")])]});
            var Q1;
            Q1=makeQuery(id+"F1.opExtrude","SWEPT_BODY",BODY,{"disambiguationData":[OSD([sQuery(id+"F0.wireOp",EDGE,"E0"),sQuery(id+"F0.wireOp",EDGE,"E12"),sQuery(id+"F0.wireOp",EDGE,"E13"),sQuery(id+"F0.wireOp",EDGE,"E18"),sQuery(id+"F0.wireOp",EDGE,"E21"),sQuery(id+"F0.wireOp",EDGE,"E22"),sQuery(id+"F0.wireOp",EDGE,"E23"),sQuery(id+"F0.wireOp",EDGE,"E24"),sQuery(id+"F0.wireOp",EDGE,"E79.right"),sQuery(id+"F0.wireOp",EDGE,"E81.bottom"),sQuery(id+"F0.wireOp",EDGE,"E81.top"),sQuery(id+"F0.wireOp",EDGE,"E81.right"),sQuery(id+"F0.wireOp",EDGE,"E82.right"),sQuery(id+"F0.wireOp",EDGE,"E83"),sQuery(id+"F0.wireOp",EDGE,"E92"),sQuery(id+"F0.wireOp",EDGE,"E93"),sQuery(id+"F0.wireOp",EDGE,"E104"),sQuery(id+"F0.wireOp",EDGE,"E107"),sQuery(id+"F0.wireOp",EDGE,"E108"),sQuery(id+"F0.wireOp",EDGE,"E109.bottom"),sQuery(id+"F0.wireOp",EDGE,"E109.right"),sQuery(id+"F0.wireOp",EDGE,"E110.bottom"),sQuery(id+"F0.wireOp",EDGE,"E111"),sQuery(id+"F0.wireOp",EDGE,"E112"),sQuery(id+"F0.wireOp",EDGE,"E127.right"),sQuery(id+"F0.wireOp",EDGE,"E128.top"),sQuery(id+"F0.wireOp",EDGE,"E128.left"),sQuery(id+"F0.wireOp",EDGE,"E136"),sQuery(id+"F0.wireOp",EDGE,"E137"),sQuery(id+"F0.wireOp",EDGE,"E138"),sQuery(id+"F0.wireOp",EDGE,"E139"),sQuery(id+"F0.wireOp",EDGE,"E142.top"),sQuery(id+"F0.wireOp",EDGE,"E168.bottom"),sQuery(id+"F0.wireOp",EDGE,"E168.right"),sQuery(id+"F0.wireOp",EDGE,"E169")])]});
            var Q2;
            Q2=makeQuery(id+"F1.opExtrude","SWEPT_BODY",BODY,{"disambiguationData":[OSD([sQuery(id+"F0.wireOp",EDGE,"E4.bottom"),sQuery(id+"F0.wireOp",EDGE,"E4.top"),sQuery(id+"F0.wireOp",EDGE,"E4.left"),sQuery(id+"F0.wireOp",EDGE,"E5.left"),sQuery(id+"F0.wireOp",EDGE,"E5.right"),sQuery(id+"F0.wireOp",EDGE,"E6.left"),sQuery(id+"F0.wireOp",EDGE,"E7.bottom"),sQuery(id+"F0.wireOp",EDGE,"E7.top"),sQuery(id+"F0.wireOp",EDGE,"E8"),sQuery(id+"F0.wireOp",EDGE,"E4.right"),sQuery(id+"F0.wireOp",EDGE,"E5.top"),sQuery(id+"F0.wireOp",EDGE,"E40"),sQuery(id+"F0.wireOp",EDGE,"E76")])]});
            var Q3;
            Q3=makeQuery(id+"F1.opExtrude","SWEPT_BODY",BODY,{"disambiguationData":[OSD([sQuery(id+"F0.wireOp",EDGE,"E29"),sQuery(id+"F0.wireOp",EDGE,"E31.top"),sQuery(id+"F0.wireOp",EDGE,"E31.left"),sQuery(id+"F0.wireOp",EDGE,"E31.right"),sQuery(id+"F0.wireOp",EDGE,"E33"),sQuery(id+"F0.wireOp",EDGE,"E34"),sQuery(id+"F0.wireOp",EDGE,"E35"),sQuery(id+"F0.wireOp",EDGE,"E36.bottom"),sQuery(id+"F0.wireOp",EDGE,"E36.top"),sQuery(id+"F0.wireOp",EDGE,"E36.left"),sQuery(id+"F0.wireOp",EDGE,"E36.right"),sQuery(id+"F0.wireOp",EDGE,"E37"),sQuery(id+"F0.wireOp",EDGE,"E38"),sQuery(id+"F0.wireOp",EDGE,"E39.bottom"),sQuery(id+"F0.wireOp",EDGE,"E39.left"),sQuery(id+"F0.wireOp",EDGE,"E39.right"),sQuery(id+"F0.wireOp",EDGE,"E46.bottom"),sQuery(id+"F0.wireOp",EDGE,"E47"),sQuery(id+"F0.wireOp",EDGE,"E52"),sQuery(id+"F0.wireOp",EDGE,"E70"),sQuery(id+"F0.wireOp",EDGE,"E71"),sQuery(id+"F0.wireOp",EDGE,"E141"),sQuery(id+"F0.wireOp",EDGE,"E146.bottom"),sQuery(id+"F0.wireOp",EDGE,"E147.left"),sQuery(id+"F0.wireOp",EDGE,"E150.bottom"),sQuery(id+"F0.wireOp",EDGE,"E163"),sQuery(id+"F0.wireOp",EDGE,"E164"),sQuery(id+"F0.wireOp",EDGE,"E165"),sQuery(id+"F0.wireOp",EDGE,"E166"),sQuery(id+"F0.wireOp",EDGE,"E167.top"),sQuery(id+"F0.wireOp",EDGE,"E167.left")])]});
            var Q4;
            Q4=makeQuery(id+"F1.opExtrude","SWEPT_BODY",BODY,{"disambiguationData":[OSD([sQuery(id+"F0.wireOp",EDGE,"E38"),sQuery(id+"F0.wireOp",EDGE,"E45"),sQuery(id+"F0.wireOp",EDGE,"E46.top"),sQuery(id+"F0.wireOp",EDGE,"E48.left"),sQuery(id+"F0.wireOp",EDGE,"E48.right"),sQuery(id+"F0.wireOp",EDGE,"E49.bottom"),sQuery(id+"F0.wireOp",EDGE,"E51"),sQuery(id+"F0.wireOp",EDGE,"E52"),sQuery(id+"F0.wireOp",EDGE,"E53.bottom"),sQuery(id+"F0.wireOp",EDGE,"E53.top"),sQuery(id+"F0.wireOp",EDGE,"E53.left"),sQuery(id+"F0.wireOp",EDGE,"E53.right"),sQuery(id+"F0.wireOp",EDGE,"E58"),sQuery(id+"F0.wireOp",EDGE,"E59"),sQuery(id+"F0.wireOp",EDGE,"E146.top"),sQuery(id+"F0.wireOp",EDGE,"E148.left"),sQuery(id+"F0.wireOp",EDGE,"E149.left"),sQuery(id+"F0.wireOp",EDGE,"E150.top")])]});
            var Q5;
            Q5=makeQuery(id+"F1.opExtrude","SWEPT_BODY",BODY,{"disambiguationData":[OSD([sQuery(id+"F0.wireOp",EDGE,"E50.bottom"),sQuery(id+"F0.wireOp",EDGE,"E50.left"),sQuery(id+"F0.wireOp",EDGE,"E50.right"),sQuery(id+"F0.wireOp",EDGE,"E54.top"),sQuery(id+"F0.wireOp",EDGE,"E54.left"),sQuery(id+"F0.wireOp",EDGE,"E54.right"),sQuery(id+"F0.wireOp",EDGE,"E55.trimOffspring"),sQuery(id+"F0.wireOp",EDGE,"E58"),sQuery(id+"F0.wireOp",EDGE,"E59"),sQuery(id+"F0.wireOp",EDGE,"E60.trimOffspring"),sQuery(id+"F0.wireOp",EDGE,"E61"),sQuery(id+"F0.wireOp",EDGE,"E62"),sQuery(id+"F0.wireOp",EDGE,"E63"),sQuery(id+"F0.wireOp",EDGE,"E64"),sQuery(id+"F0.wireOp",EDGE,"E66"),sQuery(id+"F0.wireOp",EDGE,"E67"),sQuery(id+"F0.wireOp",EDGE,"E73"),sQuery(id+"F0.wireOp",EDGE,"E84"),sQuery(id+"F0.wireOp",EDGE,"E85.right"),sQuery(id+"F0.wireOp",EDGE,"E87.top"),sQuery(id+"F0.wireOp",EDGE,"E87.left"),sQuery(id+"F0.wireOp",EDGE,"E86.right"),sQuery(id+"F0.wireOp",EDGE,"E88.top"),sQuery(id+"F0.wireOp",EDGE,"E88.left"),sQuery(id+"F0.wireOp",EDGE,"E86.left"),sQuery(id+"F0.wireOp",EDGE,"E86.bottom"),sQuery(id+"F0.wireOp",EDGE,"E89"),sQuery(id+"F0.wireOp",EDGE,"E90.bottom"),sQuery(id+"F0.wireOp",EDGE,"E90.top"),sQuery(id+"F0.wireOp",EDGE,"E91.trimOffspring"),sQuery(id+"F0.wireOp",EDGE,"E95.bottom"),sQuery(id+"F0.wireOp",EDGE,"E95.left"),sQuery(id+"F0.wireOp",EDGE,"E96.trimOffspring"),sQuery(id+"F0.wireOp",EDGE,"E97.bottom"),sQuery(id+"F0.wireOp",EDGE,"E97.top"),sQuery(id+"F0.wireOp",EDGE,"E97.left"),sQuery(id+"F0.wireOp",EDGE,"E97.right"),sQuery(id+"F0.wireOp",EDGE,"E102"),sQuery(id+"F0.wireOp",EDGE,"E114"),sQuery(id+"F0.wireOp",EDGE,"E115"),sQuery(id+"F0.wireOp",EDGE,"E143.left"),sQuery(id+"F0.wireOp",EDGE,"E144.left"),sQuery(id+"F0.wireOp",EDGE,"E144.right"),sQuery(id+"F0.wireOp",EDGE,"E145.left"),sQuery(id+"F0.wireOp",EDGE,"E145.right"),sQuery(id+"F0.wireOp",EDGE,"E148.right"),sQuery(id+"F0.wireOp",EDGE,"E149.right"),sQuery(id+"F0.wireOp",EDGE,"E152.bottom"),sQuery(id+"F0.wireOp",EDGE,"E152.top"),sQuery(id+"F0.wireOp",EDGE,"E152.left"),sQuery(id+"F0.wireOp",EDGE,"E152.right"),sQuery(id+"F0.wireOp",EDGE,"E153.bottom"),sQuery(id+"F0.wireOp",EDGE,"E153.top"),sQuery(id+"F0.wireOp",EDGE,"E153.left"),sQuery(id+"F0.wireOp",EDGE,"E153.right"),sQuery(id+"F0.wireOp",EDGE,"E154.bottom"),sQuery(id+"F0.wireOp",EDGE,"E154.top"),sQuery(id+"F0.wireOp",EDGE,"E154.right")])]});
            var Q6;
            Q6=makeQuery(id+"F1.opExtrude","SWEPT_BODY",BODY,{"disambiguationData":[OSD([sQuery(id+"F0.wireOp",EDGE,"E70"),sQuery(id+"F0.wireOp",EDGE,"E71"),sQuery(id+"F0.wireOp",EDGE,"E73"),sQuery(id+"F0.wireOp",EDGE,"E75"),sQuery(id+"F0.wireOp",EDGE,"E117"),sQuery(id+"F0.wireOp",EDGE,"E118"),sQuery(id+"F0.wireOp",EDGE,"E119"),sQuery(id+"F0.wireOp",EDGE,"E122.bottom"),sQuery(id+"F0.wireOp",EDGE,"E147.right")])]});
            var Q7;
            Q7=makeQuery(id+"F1.opExtrude","SWEPT_BODY",BODY,{"disambiguationData":[OSD([sQuery(id+"F0.wireOp",EDGE,"E90.bottom"),sQuery(id+"F0.wireOp",EDGE,"E90.top"),sQuery(id+"F0.wireOp",EDGE,"E92"),sQuery(id+"F0.wireOp",EDGE,"E93"),sQuery(id+"F0.wireOp",EDGE,"E103.right"),sQuery(id+"F0.wireOp",EDGE,"E104"),sQuery(id+"F0.wireOp",EDGE,"E105"),sQuery(id+"F0.wireOp",EDGE,"E109.top"),sQuery(id+"F0.wireOp",EDGE,"E110.top"),sQuery(id+"F0.wireOp",EDGE,"E113.trimOffspring"),sQuery(id+"F0.wireOp",EDGE,"E142.bottom"),sQuery(id+"F0.wireOp",EDGE,"E143.right")])]});
            var Q8;
            Q8=makeQuery(id+"F2.opExtrude","SWEPT_BODY",BODY,{"disambiguationData":[OSD([sQuery(id+"F0.wireOp",EDGE,"E46.bottom"),sQuery(id+"F0.wireOp",EDGE,"E46.left"),sQuery(id+"F0.wireOp",EDGE,"E46.right"),sQuery(id+"F0.wireOp",EDGE,"E46.top")])]});
            var Q9;
            Q9=makeQuery(id+"F2.opExtrude","SWEPT_BODY",BODY,{"disambiguationData":[OSD([sQuery(id+"F0.wireOp",EDGE,"E49.bottom"),sQuery(id+"F0.wireOp",EDGE,"E49.left"),sQuery(id+"F0.wireOp",EDGE,"E49.right"),sQuery(id+"F0.wireOp",EDGE,"E50.bottom")])]});
            var Q10;
            Q10=makeQuery(id+"F4.opExtrude","SWEPT_BODY",BODY,{"disambiguationData":[OSD([sQuery(id+"F3.wireOp",EDGE,"E172.0"),sQuery(id+"F3.wireOp",EDGE,"E179.bottom"),sQuery(id+"F3.wireOp",EDGE,"E179.top"),sQuery(id+"F3.wireOp",EDGE,"E179.left"),sQuery(id+"F3.wireOp",EDGE,"E179.right"),sQuery(id+"F3.wireOp",EDGE,"E176.top"),sQuery(id+"F3.wireOp",EDGE,"E176.bottom"),sQuery(id+"F3.wireOp",EDGE,"E180.right"),sQuery(id+"F3.wireOp",EDGE,"E182"),sQuery(id+"F3.wireOp",EDGE,"E184"),sQuery(id+"F3.wireOp",EDGE,"E185"),sQuery(id+"F3.wireOp",EDGE,"E186"),sQuery(id+"F3.wireOp",EDGE,"E187"),sQuery(id+"F3.wireOp",EDGE,"E188"),sQuery(id+"F3.wireOp",EDGE,"E189")])]});
            var Q11;
            Q11=makeQuery(id+"F6.opExtrude","SWEPT_BODY",BODY,{"disambiguationData":[OSD([sQuery(id+"F5.wireOp",EDGE,"E191.bottom"),sQuery(id+"F5.wireOp",EDGE,"E191.top"),sQuery(id+"F5.wireOp",EDGE,"E191.left"),sQuery(id+"F5.wireOp",EDGE,"E191.right")])]});
            var Q12;
            Q12=makeQuery(id+"F6.opExtrude","SWEPT_BODY",BODY,{"disambiguationData":[OSD([sQuery(id+"F5.wireOp",EDGE,"E192.bottom"),sQuery(id+"F5.wireOp",EDGE,"E192.top"),sQuery(id+"F5.wireOp",EDGE,"E192.left"),sQuery(id+"F5.wireOp",EDGE,"E192.right")])]});
            var Q13;
            Q13=makeQuery(id+"F8.opExtrude","SWEPT_BODY",BODY,{"disambiguationData":[OSD([sQuery(id+"F7.wireOp",EDGE,"E194.bottom"),sQuery(id+"F7.wireOp",EDGE,"E194.top"),sQuery(id+"F7.wireOp",EDGE,"E194.left"),sQuery(id+"F7.wireOp",EDGE,"E194.right")])]});
            var Q14;
            Q14=makeQuery(id+"F12.opExtrude","SWEPT_BODY",BODY,{"disambiguationData":[OSD([sQuery(id+"F11.wireOp",EDGE,"E206.bottom"),sQuery(id+"F11.wireOp",EDGE,"E206.top"),sQuery(id+"F11.wireOp",EDGE,"E206.left"),sQuery(id+"F11.wireOp",EDGE,"E206.right")])]});
            var Q15;
            Q15=makeQuery(id+"F12.opExtrude","SWEPT_BODY",BODY,{"disambiguationData":[OSD([sQuery(id+"F11.wireOp",EDGE,"E207.bottom"),sQuery(id+"F11.wireOp",EDGE,"E207.top"),sQuery(id+"F11.wireOp",EDGE,"E207.left"),sQuery(id+"F11.wireOp",EDGE,"E207.right")])]});
            var Q16;
            Q16=makeQuery(id+"F14.opExtrude","SWEPT_BODY",BODY,{"disambiguationData":[OSD([sQuery(id+"F13.wireOp",EDGE,"E210.bottom"),sQuery(id+"F13.wireOp",EDGE,"E210.top"),sQuery(id+"F13.wireOp",EDGE,"E210.left"),sQuery(id+"F13.wireOp",EDGE,"E210.right")])]});
            var Q17;
            Q17=makeQuery(id+"F16.opExtrude","SWEPT_BODY",BODY,{"disambiguationData":[OSD([sQuery(id+"F15.wireOp",EDGE,"E213.bottom"),sQuery(id+"F15.wireOp",EDGE,"E213.top"),sQuery(id+"F15.wireOp",EDGE,"E213.left"),sQuery(id+"F15.wireOp",EDGE,"E213.right")])]});
            var Q18;
            Q18=makeQuery(id+"F18.opExtrude","SWEPT_BODY",BODY,{"disambiguationData":[OSD([sQuery(id+"F17.wireOp",EDGE,"E216.bottom"),sQuery(id+"F17.wireOp",EDGE,"E216.top"),sQuery(id+"F17.wireOp",EDGE,"E216.left"),sQuery(id+"F17.wireOp",EDGE,"E216.right")])]});
            var Q19;
            Q19=makeQuery(id+"F20.opExtrude","SWEPT_BODY",BODY,{"disambiguationData":[OSD([sQuery(id+"F19.wireOp",EDGE,"E217.0.0"),sQuery(id+"F19.wireOp",EDGE,"E217.0.1"),sQuery(id+"F19.wireOp",EDGE,"E217.0.2"),sQuery(id+"F19.wireOp",EDGE,"E217.0.3"),sQuery(id+"F19.wireOp",EDGE,"E218.bottom"),sQuery(id+"F19.wireOp",EDGE,"E218.top"),sQuery(id+"F19.wireOp",EDGE,"E218.right")])]});
            var Q20;
            Q20=makeQuery(id+"F22.opExtrude","SWEPT_BODY",BODY,{"disambiguationData":[OSD([sQuery(id+"F21.wireOp",EDGE,"E221.bottom"),sQuery(id+"F21.wireOp",EDGE,"E221.top"),sQuery(id+"F21.wireOp",EDGE,"E221.left"),sQuery(id+"F21.wireOp",EDGE,"E221.right")])]});
            var Q21;
            Q21=makeQuery(id+"F24.opExtrude","SWEPT_BODY",BODY,{"disambiguationData":[OSD([sQuery(id+"F23.wireOp",EDGE,"E226.bottom"),sQuery(id+"F23.wireOp",EDGE,"E226.top"),sQuery(id+"F23.wireOp",EDGE,"E226.left"),sQuery(id+"F23.wireOp",EDGE,"E226.right")])]});
            var Q22;
            Q22=makeQuery(id+"F24.opExtrude","SWEPT_BODY",BODY,{"disambiguationData":[OSD([sQuery(id+"F23.wireOp",EDGE,"E227.bottom"),sQuery(id+"F23.wireOp",EDGE,"E227.top"),sQuery(id+"F23.wireOp",EDGE,"E227.left"),sQuery(id+"F23.wireOp",EDGE,"E227.right")])]});
            var Q23;
            Q23=makeQuery(id+"F26.opExtrude","SWEPT_BODY",BODY,{"disambiguationData":[OSD([sQuery(id+"F25.wireOp",EDGE,"E230.bottom"),sQuery(id+"F25.wireOp",EDGE,"E230.top"),sQuery(id+"F25.wireOp",EDGE,"E230.left"),sQuery(id+"F25.wireOp",EDGE,"E230.right")])]});
            var Q24;
            Q24=makeQuery(id+"F28.opExtrude","SWEPT_BODY",BODY,{"disambiguationData":[OSD([sQuery(id+"F27.wireOp",EDGE,"E234.bottom"),sQuery(id+"F27.wireOp",EDGE,"E234.top"),sQuery(id+"F27.wireOp",EDGE,"E234.left"),sQuery(id+"F27.wireOp",EDGE,"E234.right")])]});
            var Q25;
            Q25=makeQuery(id+"F2.opExtrude","SWEPT_BODY",BODY,{"disambiguationData":[OSD([sQuery(id+"F0.wireOp",EDGE,"E7.bottom"),sQuery(id+"F0.wireOp",EDGE,"E7.top"),sQuery(id+"F0.wireOp",EDGE,"E7.right"),sQuery(id+"F0.wireOp",EDGE,"E8")])]});
            var Q26;
            Q26=makeQuery(id+"F8.opExtrude","SWEPT_BODY",BODY,{"disambiguationData":[OSD([sQuery(id+"F7.wireOp",EDGE,"E193.bottom"),sQuery(id+"F7.wireOp",EDGE,"E193.top"),sQuery(id+"F7.wireOp",EDGE,"E193.left"),sQuery(id+"F7.wireOp",EDGE,"E193.right")])]});
            var Q27;
            Q27=makeQuery(id+"F30.opExtrude","SWEPT_FACE",FACE,{"disambiguationData":[OSD([sQuery(id+"F29.wireOp",EDGE,"E235.right")])]});
            mirror(context, id + "F31", {"entities" : qUnion([Q0, Q1, Q2, Q3, Q4, Q5, Q6, Q7, Q8, Q9, Q10, Q11, Q12, Q13, Q14, Q15, Q16, Q17, Q18, Q19, Q20, Q21, Q22, Q23, Q24, Q25, Q26]), "mirrorPlane" : qUnion([Q27])});
        }
    });
